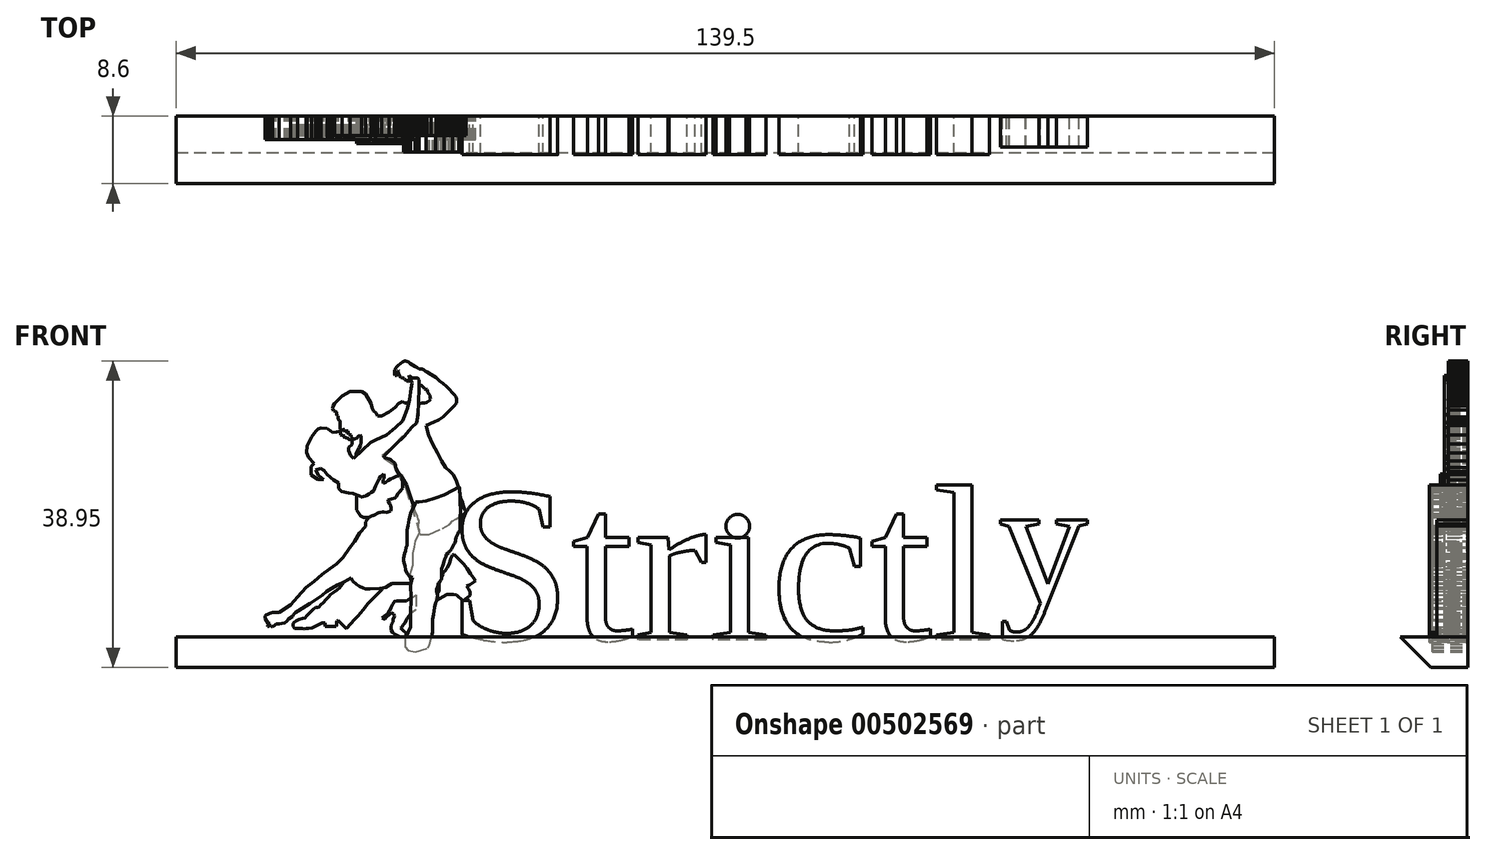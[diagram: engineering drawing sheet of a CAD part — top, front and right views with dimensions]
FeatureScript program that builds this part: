
annotation { "Feature Type Name" : "Feature", "Feature Type Description" : "" }
export const myFeature = defineFeature(function(context is Context, id is Id, definition is map)
    precondition{}
    {
        {
            var Q0;
            Q0=qCreatedBy(makeId("Front.planeOp"),FACE);
            var sketch = newSketch(context, id + "F0", { "sketchPlane" : qUnion([Q0])});
            skLineSegment(sketch, "E0", {"start": v(-53.06, 27.82) * mm, "end": v(-53.58, 27.08) * mm});
            skLineSegment(sketch, "E1", {"start": v(-53.58, 27.08) * mm, "end": v(-54.13, 25.96) * mm});
            skLineSegment(sketch, "E2", {"start": v(-54.13, 25.96) * mm, "end": v(-54.19, 25.15) * mm});
            skLineSegment(sketch, "E3", {"start": v(-54.19, 25.15) * mm, "end": v(-53.94, 24.5) * mm});
            skLineSegment(sketch, "E4", {"start": v(-53.94, 24.5) * mm, "end": v(-53.26, 23.7) * mm});
            skLineSegment(sketch, "E5", {"start": v(-53.26, 23.7) * mm, "end": v(-53.64, 23.37) * mm});
            skLineSegment(sketch, "E6", {"start": v(-53.64, 23.37) * mm, "end": v(-53.64, 22.67) * mm});
            skLineSegment(sketch, "E7", {"start": v(-53.64, 22.67) * mm, "end": v(-53.64, 22.27) * mm});
            skLineSegment(sketch, "E8", {"start": v(-53.64, 22.27) * mm, "end": v(-52.72, 21.68) * mm});
            skLineSegment(sketch, "E9", {"start": v(-52.72, 21.68) * mm, "end": v(-52.02, 21.68) * mm});
            skLineSegment(sketch, "E10", {"start": v(-52.02, 21.68) * mm, "end": v(-52.66, 22.2) * mm});
            skLineSegment(sketch, "E11", {"start": v(-52.66, 22.2) * mm, "end": v(-53.02, 22.89) * mm});
            skLineSegment(sketch, "E12", {"start": v(-53.02, 22.89) * mm, "end": v(-52.43, 23.06) * mm});
            skLineSegment(sketch, "E13", {"start": v(-52.43, 23.06) * mm, "end": v(-51.95, 22.82) * mm});
            skLineSegment(sketch, "E14", {"start": v(-51.95, 22.82) * mm, "end": v(-51.6, 22.35) * mm});
            skLineSegment(sketch, "E15", {"start": v(-51.6, 22.35) * mm, "end": v(-50.73, 21.64) * mm});
            skLineSegment(sketch, "E16", {"start": v(-50.73, 21.64) * mm, "end": v(-50.1, 21.27) * mm});
            skLineSegment(sketch, "E17", {"start": v(-50.1, 21.27) * mm, "end": v(-50.1, 20.97) * mm});
            skLineSegment(sketch, "E18", {"start": v(-50.1, 20.97) * mm, "end": v(-50.1, 20.53) * mm});
            skLineSegment(sketch, "E19", {"start": v(-50.1, 20.53) * mm, "end": v(-49.73, 20.2) * mm});
            skLineSegment(sketch, "E20", {"start": v(-49.73, 20.2) * mm, "end": v(-48.85, 20) * mm});
            skLineSegment(sketch, "E21", {"start": v(-48.85, 20) * mm, "end": v(-48.26, 19.9) * mm});
            skLineSegment(sketch, "E22", {"start": v(-48.26, 19.9) * mm, "end": v(-47.76, 19.67) * mm});
            skLineSegment(sketch, "E23", {"start": v(-47.76, 19.67) * mm, "end": v(-47.24, 19.46) * mm});
            skLineSegment(sketch, "E24", {"start": v(-47.24, 19.46) * mm, "end": v(-46.67, 19.58) * mm});
            skLineSegment(sketch, "E25", {"start": v(-46.67, 19.58) * mm, "end": v(-45.62, 20.23) * mm});
            skLineSegment(sketch, "E26", {"start": v(-45.62, 20.23) * mm, "end": v(-45.36, 20.9) * mm});
            skLineSegment(sketch, "E27", {"start": v(-45.36, 20.9) * mm, "end": v(-44.92, 21.82) * mm});
            skLineSegment(sketch, "E28", {"start": v(-44.92, 21.82) * mm, "end": v(-44.46, 22.36) * mm});
            skLineSegment(sketch, "E29", {"start": v(-44.46, 22.36) * mm, "end": v(-44.32, 22.24) * mm});
            skLineSegment(sketch, "E30", {"start": v(-44.32, 21.2) * mm, "end": v(-43.25, 21.86) * mm});
            skLineSegment(sketch, "E31", {"start": v(-43.25, 21.86) * mm, "end": v(-42.36, 22.24) * mm});
            skLineSegment(sketch, "E32", {"start": v(-42.36, 22.24) * mm, "end": v(-42.79, 23.01) * mm});
            skLineSegment(sketch, "E33", {"start": v(-42.79, 23.01) * mm, "end": v(-42.95, 23.7) * mm});
            skLineSegment(sketch, "E34", {"start": v(-42.95, 23.7) * mm, "end": v(-43.5, 24.23) * mm});
            skLineSegment(sketch, "E35", {"start": v(-43.5, 24.23) * mm, "end": v(-44.32, 24.46) * mm});
            skLineSegment(sketch, "E36", {"start": v(-44.32, 24.46) * mm, "end": v(-44.36, 24.68) * mm});
            skLineSegment(sketch, "E37", {"start": v(-44.36, 24.68) * mm, "end": v(-42.92, 26.08) * mm});
            skLineSegment(sketch, "E38", {"start": v(-42.92, 26.08) * mm, "end": v(-41.73, 27.23) * mm});
            skLineSegment(sketch, "E39", {"start": v(-41.73, 27.23) * mm, "end": v(-40.85, 28.27) * mm});
            skLineSegment(sketch, "E40", {"start": v(-40.85, 28.27) * mm, "end": v(-40.2, 28.88) * mm});
            skLineSegment(sketch, "E41", {"start": v(-40.2, 28.88) * mm, "end": v(-40.01, 29.93) * mm});
            skLineSegment(sketch, "E42", {"start": v(-40.01, 29.93) * mm, "end": v(-39.92, 33.22) * mm});
            skLineSegment(sketch, "E43", {"start": v(-39.92, 33.22) * mm, "end": v(-39.89, 34.32) * mm});
            skLineSegment(sketch, "E44", {"start": v(-39.89, 34.32) * mm, "end": v(-40.01, 34.54) * mm});
            skLineSegment(sketch, "E45", {"start": v(-40.01, 34.54) * mm, "end": v(-40.14, 34.59) * mm});
            skLineSegment(sketch, "E46", {"start": v(-40.14, 34.59) * mm, "end": v(-40.75, 34.61) * mm});
            skLineSegment(sketch, "E47", {"start": v(-40.75, 34.61) * mm, "end": v(-41.19, 34.9) * mm});
            skLineSegment(sketch, "E48", {"start": v(-41.19, 34.9) * mm, "end": v(-41.08, 34.46) * mm});
            skLineSegment(sketch, "E49", {"start": v(-41.08, 34.46) * mm, "end": v(-40.98, 34.36) * mm});
            skLineSegment(sketch, "E50", {"start": v(-40.98, 34.36) * mm, "end": v(-40.77, 33.93) * mm});
            skLineSegment(sketch, "E51", {"start": v(-40.77, 33.93) * mm, "end": v(-40.88, 33.22) * mm});
            skLineSegment(sketch, "E52", {"start": v(-40.88, 33.22) * mm, "end": v(-41.1, 31.86) * mm});
            skLineSegment(sketch, "E53", {"start": v(-41.1, 31.86) * mm, "end": v(-41.37, 30.75) * mm});
            skLineSegment(sketch, "E54", {"start": v(-41.37, 30.75) * mm, "end": v(-41.72, 29.75) * mm});
            skLineSegment(sketch, "E55", {"start": v(-41.72, 29.75) * mm, "end": v(-41.98, 29.15) * mm});
            skLineSegment(sketch, "E56", {"start": v(-41.98, 29.15) * mm, "end": v(-42.87, 28.32) * mm});
            skLineSegment(sketch, "E57", {"start": v(-42.87, 28.32) * mm, "end": v(-44.05, 27.37) * mm});
            skLineSegment(sketch, "E58", {"start": v(-44.05, 27.37) * mm, "end": v(-45.4, 26.73) * mm});
            skLineSegment(sketch, "E59", {"start": v(-45.4, 26.73) * mm, "end": v(-46.05, 26.38) * mm});
            skLineSegment(sketch, "E60", {"start": v(-46.05, 26.38) * mm, "end": v(-46.93, 25.56) * mm});
            skLineSegment(sketch, "E61", {"start": v(-46.93, 25.56) * mm, "end": v(-47.64, 24.9) * mm});
            skLineSegment(sketch, "E62", {"start": v(-47.64, 24.9) * mm, "end": v(-48.21, 24.35) * mm});
            skLineSegment(sketch, "E63", {"start": v(-48.21, 24.35) * mm, "end": v(-48.6, 24.76) * mm});
            skLineSegment(sketch, "E64", {"start": v(-48.6, 24.76) * mm, "end": v(-48.82, 25.34) * mm});
            skLineSegment(sketch, "E65", {"start": v(-48.82, 25.34) * mm, "end": v(-48.82, 25.78) * mm});
            skLineSegment(sketch, "E66", {"start": v(-48.82, 25.78) * mm, "end": v(-48.43, 26.16) * mm});
            skLineSegment(sketch, "E67", {"start": v(-48.43, 26.16) * mm, "end": v(-48.38, 26.51) * mm});
            skLineSegment(sketch, "E68", {"start": v(-48.38, 26.51) * mm, "end": v(-48.47, 26.69) * mm});
            skLineSegment(sketch, "E69", {"start": v(-48.47, 26.69) * mm, "end": v(-48.78, 26.74) * mm});
            skLineSegment(sketch, "E70", {"start": v(-48.78, 26.74) * mm, "end": v(-48.9, 26.87) * mm});
            skLineSegment(sketch, "E71", {"start": v(-48.9, 26.87) * mm, "end": v(-49.23, 27.04) * mm});
            skLineSegment(sketch, "E72", {"start": v(-49.23, 27.04) * mm, "end": v(-49.37, 26.9) * mm});
            skLineSegment(sketch, "E73", {"start": v(-49.37, 26.9) * mm, "end": v(-49.4, 27.21) * mm});
            skLineSegment(sketch, "E74", {"start": v(-49.4, 27.21) * mm, "end": v(-49.84, 27.32) * mm});
            skLineSegment(sketch, "E75", {"start": v(-49.84, 27.32) * mm, "end": v(-49.85, 27.76) * mm});
            skLineSegment(sketch, "E76", {"start": v(-49.85, 27.76) * mm, "end": v(-50.03, 27.79) * mm});
            skLineSegment(sketch, "E77", {"start": v(-50.4, 27.73) * mm, "end": v(-50.88, 27.63) * mm});
            skLineSegment(sketch, "E78", {"start": v(-50.88, 27.63) * mm, "end": v(-51.2, 27.89) * mm});
            skLineSegment(sketch, "E79", {"start": v(-51.2, 27.89) * mm, "end": v(-51.55, 28.14) * mm});
            skLineSegment(sketch, "E80", {"start": v(-51.55, 28.14) * mm, "end": v(-52.32, 28.23) * mm});
            skLineSegment(sketch, "E81", {"start": v(-52.32, 28.23) * mm, "end": v(-52.7, 28.13) * mm});
            skLineSegment(sketch, "E82", {"start": v(-52.7, 28.13) * mm, "end": v(-53.06, 27.82) * mm});
            skLineSegment(sketch, "E83", {"start": v(-50.03, 27.79) * mm, "end": v(-50.4, 27.73) * mm});
            skLineSegment(sketch, "E84", {"start": v(-44.32, 21.2) * mm, "end": v(-44.5, 21.2) * mm});
            skLineSegment(sketch, "E85", {"start": v(-44.5, 21.2) * mm, "end": v(-44.5, 21.47) * mm});
            skLineSegment(sketch, "E86", {"start": v(-44.5, 21.47) * mm, "end": v(-44.5, 21.6) * mm});
            skLineSegment(sketch, "E87", {"start": v(-44.5, 21.6) * mm, "end": v(-44.33, 21.82) * mm});
            skLineSegment(sketch, "E88", {"start": v(-44.33, 21.82) * mm, "end": v(-44.32, 22.24) * mm});
            skSolve(sketch);
        }
        {
            var Q0;
            Q0=makeQuery(id+"F0.imprint","IMPRINT",FACE,{"disambiguationData":[TD([[makeQuery(id+"F0.imprint","IMPRINT",EDGE,{"derivedFrom":sQuery(id+"F0.wireOp",EDGE,"E0")}),1.0]])]});
            extrude(context, id + "F1", {"entities" : qUnion([Q0]), "depth" : 3 * mm, "offsetDistance" : 25 * mm});
        }
        {
            var Q0;
            Q0=qCreatedBy(makeId("Front.planeOp"),FACE);
            var sketch = newSketch(context, id + "F2", { "sketchPlane" : qUnion([Q0])});
            skLineSegment(sketch, "E89", {"start": v(-46.21, 17.05) * mm, "end": v(-46.69, 16.29) * mm});
            skLineSegment(sketch, "E90", {"start": v(-46.69, 16.29) * mm, "end": v(-46.69, 15.72) * mm});
            skLineSegment(sketch, "E91", {"start": v(-46.69, 15.72) * mm, "end": v(-47.43, 14.93) * mm});
            skLineSegment(sketch, "E92", {"start": v(-47.43, 14.93) * mm, "end": v(-48.1, 13.82) * mm});
            skLineSegment(sketch, "E93", {"start": v(-48.1, 13.82) * mm, "end": v(-48.7, 12.97) * mm});
            skLineSegment(sketch, "E94", {"start": v(-48.7, 12.97) * mm, "end": v(-49.56, 11.77) * mm});
            skLineSegment(sketch, "E95", {"start": v(-49.56, 11.77) * mm, "end": v(-50.37, 10.98) * mm});
            skLineSegment(sketch, "E96", {"start": v(-50.37, 10.98) * mm, "end": v(-51.28, 10.32) * mm});
            skLineSegment(sketch, "E97", {"start": v(-51.28, 10.32) * mm, "end": v(-52.23, 9.62) * mm});
            skLineSegment(sketch, "E98", {"start": v(-52.23, 9.62) * mm, "end": v(-53.24, 8.75) * mm});
            skLineSegment(sketch, "E99", {"start": v(-53.24, 8.75) * mm, "end": v(-54.28, 7.99) * mm});
            skLineSegment(sketch, "E100", {"start": v(-54.28, 7.99) * mm, "end": v(-55.36, 6.8) * mm});
            skLineSegment(sketch, "E101", {"start": v(-55.36, 6.8) * mm, "end": v(-56.24, 5.77) * mm});
            skLineSegment(sketch, "E102", {"start": v(-56.24, 5.77) * mm, "end": v(-57.11, 5.18) * mm});
            skLineSegment(sketch, "E103", {"start": v(-57.11, 5.18) * mm, "end": v(-57.7, 4.79) * mm});
            skLineSegment(sketch, "E104", {"start": v(-57.7, 4.79) * mm, "end": v(-57.98, 4.79) * mm});
            skLineSegment(sketch, "E105", {"start": v(-57.98, 4.79) * mm, "end": v(-58.5, 4.79) * mm});
            skLineSegment(sketch, "E106", {"start": v(-58.5, 4.79) * mm, "end": v(-58.9, 4.7) * mm});
            skLineSegment(sketch, "E107", {"start": v(-58.9, 4.7) * mm, "end": v(-59.11, 4.56) * mm});
            skLineSegment(sketch, "E108", {"start": v(-59.11, 4.56) * mm, "end": v(-59.33, 4.5) * mm});
            skLineSegment(sketch, "E109", {"start": v(-59.33, 4.5) * mm, "end": v(-59.48, 4.39) * mm});
            skLineSegment(sketch, "E110", {"start": v(-59.48, 4.39) * mm, "end": v(-59.48, 4.02) * mm});
            skLineSegment(sketch, "E111", {"start": v(-59.48, 4.02) * mm, "end": v(-59.16, 3.54) * mm});
            skLineSegment(sketch, "E112", {"start": v(-59.16, 3.54) * mm, "end": v(-59.05, 3.38) * mm});
            skLineSegment(sketch, "E113", {"start": v(-59.05, 3.38) * mm, "end": v(-58.83, 3.38) * mm});
            skLineSegment(sketch, "E114", {"start": v(-58.83, 3.38) * mm, "end": v(-59.17, 3.16) * mm});
            skLineSegment(sketch, "E115", {"start": v(-59.17, 3.16) * mm, "end": v(-59.12, 3.01) * mm});
            skLineSegment(sketch, "E116", {"start": v(-59.12, 3.01) * mm, "end": v(-58.95, 3.01) * mm});
            skLineSegment(sketch, "E117", {"start": v(-58.95, 3.01) * mm, "end": v(-58.8, 3.12) * mm});
            skLineSegment(sketch, "E118", {"start": v(-58.8, 3.12) * mm, "end": v(-58.72, 3.16) * mm});
            skLineSegment(sketch, "E119", {"start": v(-58.72, 3.16) * mm, "end": v(-58.65, 3.01) * mm});
            skLineSegment(sketch, "E120", {"start": v(-58.65, 3.01) * mm, "end": v(-58.5, 2.97) * mm});
            skLineSegment(sketch, "E121", {"start": v(-58.5, 2.97) * mm, "end": v(-58.33, 3.07) * mm});
            skLineSegment(sketch, "E122", {"start": v(-58.33, 3.07) * mm, "end": v(-58.04, 3.32) * mm});
            skLineSegment(sketch, "E123", {"start": v(-58.04, 3.32) * mm, "end": v(-57.65, 3.37) * mm});
            skLineSegment(sketch, "E124", {"start": v(-57.65, 3.37) * mm, "end": v(-56.98, 3.5) * mm});
            skLineSegment(sketch, "E125", {"start": v(-56.98, 3.5) * mm, "end": v(-56.7, 3.64) * mm});
            skLineSegment(sketch, "E126", {"start": v(-56.7, 3.64) * mm, "end": v(-56.45, 3.99) * mm});
            skLineSegment(sketch, "E127", {"start": v(-56.45, 3.99) * mm, "end": v(-55.97, 4.3) * mm});
            skLineSegment(sketch, "E128", {"start": v(-55.97, 4.3) * mm, "end": v(-55.86, 4.56) * mm});
            skLineSegment(sketch, "E129", {"start": v(-55.86, 4.56) * mm, "end": v(-55.57, 4.82) * mm});
            skLineSegment(sketch, "E130", {"start": v(-55.57, 4.82) * mm, "end": v(-55.27, 5) * mm});
            skLineSegment(sketch, "E131", {"start": v(-55.27, 5) * mm, "end": v(-53.75, 5.93) * mm});
            skLineSegment(sketch, "E132", {"start": v(-53.75, 5.93) * mm, "end": v(-53.02, 6.42) * mm});
            skLineSegment(sketch, "E133", {"start": v(-53.02, 6.42) * mm, "end": v(-52.24, 6.94) * mm});
            skLineSegment(sketch, "E134", {"start": v(-52.24, 6.94) * mm, "end": v(-51.63, 7.46) * mm});
            skLineSegment(sketch, "E135", {"start": v(-51.63, 7.46) * mm, "end": v(-51, 7.88) * mm});
            skLineSegment(sketch, "E136", {"start": v(-51, 7.88) * mm, "end": v(-50.27, 8.3) * mm});
            skLineSegment(sketch, "E137", {"start": v(-50.27, 8.3) * mm, "end": v(-49.73, 8.54) * mm});
            skLineSegment(sketch, "E138", {"start": v(-49.73, 8.54) * mm, "end": v(-49.4, 8.68) * mm});
            skLineSegment(sketch, "E139", {"start": v(-49.4, 8.68) * mm, "end": v(-48.51, 9.16) * mm});
            skLineSegment(sketch, "E140", {"start": v(-48.51, 9.16) * mm, "end": v(-48.3, 8.78) * mm});
            skLineSegment(sketch, "E141", {"start": v(-48.3, 8.78) * mm, "end": v(-47.85, 8.37) * mm});
            skLineSegment(sketch, "E142", {"start": v(-47.85, 8.37) * mm, "end": v(-47.48, 8.12) * mm});
            skLineSegment(sketch, "E143", {"start": v(-47.48, 8.12) * mm, "end": v(-47.03, 7.94) * mm});
            skLineSegment(sketch, "E144", {"start": v(-47.03, 7.94) * mm, "end": v(-46.67, 7.81) * mm});
            skLineSegment(sketch, "E145", {"start": v(-46.67, 7.81) * mm, "end": v(-46.1, 7.81) * mm});
            skLineSegment(sketch, "E146", {"start": v(-46.1, 7.81) * mm, "end": v(-44.84, 7.86) * mm});
            skLineSegment(sketch, "E147", {"start": v(-44.84, 7.86) * mm, "end": v(-44.17, 8) * mm});
            skLineSegment(sketch, "E148", {"start": v(-44.17, 8) * mm, "end": v(-43.66, 8.27) * mm});
            skLineSegment(sketch, "E149", {"start": v(-43.66, 8.27) * mm, "end": v(-43.35, 8.48) * mm});
            skLineSegment(sketch, "E150", {"start": v(-43.35, 8.48) * mm, "end": v(-42.47, 8.48) * mm});
            skLineSegment(sketch, "E151", {"start": v(-42.47, 8.48) * mm, "end": v(-41.17, 8.48) * mm});
            skLineSegment(sketch, "E152", {"start": v(-41.17, 8.48) * mm, "end": v(-40.8, 8.38) * mm});
            skLineSegment(sketch, "E153", {"start": v(-40.8, 8.38) * mm, "end": v(-40.89, 8.88) * mm});
            skLineSegment(sketch, "E154", {"start": v(-40.89, 8.88) * mm, "end": v(-41.02, 9.33) * mm});
            skLineSegment(sketch, "E155", {"start": v(-41.02, 9.33) * mm, "end": v(-40.9, 10) * mm});
            skLineSegment(sketch, "E156", {"start": v(-40.9, 10) * mm, "end": v(-40.67, 10.82) * mm});
            skLineSegment(sketch, "E157", {"start": v(-40.67, 10.82) * mm, "end": v(-40.67, 11.56) * mm});
            skLineSegment(sketch, "E158", {"start": v(-40.67, 11.56) * mm, "end": v(-40.67, 12.27) * mm});
            skLineSegment(sketch, "E159", {"start": v(-40.67, 12.27) * mm, "end": v(-40.5, 13.12) * mm});
            skLineSegment(sketch, "E160", {"start": v(-40.5, 13.12) * mm, "end": v(-40.33, 13.9) * mm});
            skLineSegment(sketch, "E161", {"start": v(-40.33, 13.9) * mm, "end": v(-39.8, 15) * mm});
            skLineSegment(sketch, "E162", {"start": v(-39.8, 15) * mm, "end": v(-39.8, 15.3) * mm});
            skLineSegment(sketch, "E163", {"start": v(-39.8, 15.3) * mm, "end": v(-39.98, 15.54) * mm});
            skLineSegment(sketch, "E164", {"start": v(-39.98, 15.54) * mm, "end": v(-39.98, 15.89) * mm});
            skLineSegment(sketch, "E165", {"start": v(-39.98, 15.89) * mm, "end": v(-39.89, 16.17) * mm});
            skLineSegment(sketch, "E166", {"start": v(-39.89, 16.17) * mm, "end": v(-39.89, 16.5) * mm});
            skLineSegment(sketch, "E167", {"start": v(-39.89, 16.5) * mm, "end": v(-40.02, 16.7) * mm});
            skLineSegment(sketch, "E168", {"start": v(-40.02, 16.7) * mm, "end": v(-40.11, 17.01) * mm});
            skLineSegment(sketch, "E169", {"start": v(-40.11, 17.01) * mm, "end": v(-40.4, 17.72) * mm});
            skLineSegment(sketch, "E170", {"start": v(-40.4, 17.72) * mm, "end": v(-40.69, 18.51) * mm});
            skLineSegment(sketch, "E171", {"start": v(-40.69, 18.51) * mm, "end": v(-40.88, 19.14) * mm});
            skLineSegment(sketch, "E172", {"start": v(-40.88, 19.14) * mm, "end": v(-41.11, 19.88) * mm});
            skLineSegment(sketch, "E173", {"start": v(-41.11, 19.88) * mm, "end": v(-41.33, 20.55) * mm});
            skLineSegment(sketch, "E174", {"start": v(-41.33, 20.55) * mm, "end": v(-41.47, 21.02) * mm});
            skLineSegment(sketch, "E175", {"start": v(-41.47, 21.02) * mm, "end": v(-41.8, 21.5) * mm});
            skLineSegment(sketch, "E176", {"start": v(-41.8, 21.5) * mm, "end": v(-42.09, 21.93) * mm});
            skLineSegment(sketch, "E177", {"start": v(-42.09, 21.93) * mm, "end": v(-41.98, 20.95) * mm});
            skLineSegment(sketch, "E178", {"start": v(-41.98, 20.95) * mm, "end": v(-41.98, 20.52) * mm});
            skLineSegment(sketch, "E179", {"start": v(-41.98, 20.52) * mm, "end": v(-42.34, 20.27) * mm});
            skLineSegment(sketch, "E180", {"start": v(-42.34, 20.27) * mm, "end": v(-42.73, 19.69) * mm});
            skLineSegment(sketch, "E181", {"start": v(-42.73, 19.69) * mm, "end": v(-42.97, 19.36) * mm});
            skLineSegment(sketch, "E182", {"start": v(-42.97, 19.36) * mm, "end": v(-43.46, 19.2) * mm});
            skLineSegment(sketch, "E183", {"start": v(-43.46, 19.2) * mm, "end": v(-43.9, 19.07) * mm});
            skLineSegment(sketch, "E184", {"start": v(-43.9, 19.07) * mm, "end": v(-43.61, 18.63) * mm});
            skLineSegment(sketch, "E185", {"start": v(-43.61, 18.63) * mm, "end": v(-43.48, 18.22) * mm});
            skLineSegment(sketch, "E186", {"start": v(-43.48, 18.22) * mm, "end": v(-43.48, 17.8) * mm});
            skLineSegment(sketch, "E187", {"start": v(-43.48, 17.8) * mm, "end": v(-43.67, 17.68) * mm});
            skLineSegment(sketch, "E188", {"start": v(-43.67, 17.68) * mm, "end": v(-43.96, 17.56) * mm});
            skLineSegment(sketch, "E189", {"start": v(-43.96, 17.56) * mm, "end": v(-44.45, 17.56) * mm});
            skLineSegment(sketch, "E190", {"start": v(-44.45, 17.56) * mm, "end": v(-44.95, 17.57) * mm});
            skLineSegment(sketch, "E191", {"start": v(-44.95, 17.57) * mm, "end": v(-45.2, 17.4) * mm});
            skLineSegment(sketch, "E192", {"start": v(-45.2, 17.4) * mm, "end": v(-45.6, 17.13) * mm});
            skLineSegment(sketch, "E193", {"start": v(-45.6, 17.13) * mm, "end": v(-46.21, 17.05) * mm});
            skSolve(sketch);
        }
        {
            var Q0;
            Q0=makeQuery(id+"F2.imprint","IMPRINT",FACE,{"disambiguationData":[TD([[makeQuery(id+"F2.imprint","IMPRINT",EDGE,{"derivedFrom":sQuery(id+"F2.wireOp",EDGE,"E89")}),1.0]])]});
            extrude(context, id + "F3", {"entities" : qUnion([Q0]), "depth" : 3 * mm, "offsetDistance" : 25 * mm});
        }
        {
            var Q0;
            Q0=qCreatedBy(makeId("Front.planeOp"),FACE);
            var sketch = newSketch(context, id + "F4", { "sketchPlane" : qUnion([Q0])});
            skLineSegment(sketch, "E194", {"start": v(-40.43, 5.05) * mm, "end": v(-40.9, 4.7) * mm});
            skLineSegment(sketch, "E195", {"start": v(-40.9, 4.7) * mm, "end": v(-41.22, 4.32) * mm});
            skLineSegment(sketch, "E196", {"start": v(-41.22, 4.32) * mm, "end": v(-41.42, 4.06) * mm});
            skLineSegment(sketch, "E197", {"start": v(-41.42, 4.06) * mm, "end": v(-41.55, 3.76) * mm});
            skLineSegment(sketch, "E198", {"start": v(-41.55, 3.76) * mm, "end": v(-41.7, 3.45) * mm});
            skLineSegment(sketch, "E199", {"start": v(-41.7, 3.45) * mm, "end": v(-41.92, 3.2) * mm});
            skLineSegment(sketch, "E200", {"start": v(-41.92, 3.2) * mm, "end": v(-42.08, 2.97) * mm});
            skLineSegment(sketch, "E201", {"start": v(-42.08, 2.97) * mm, "end": v(-42.22, 2.83) * mm});
            skLineSegment(sketch, "E202", {"start": v(-42.22, 2.83) * mm, "end": v(-42.16, 2.76) * mm});
            skLineSegment(sketch, "E203", {"start": v(-42.16, 2.76) * mm, "end": v(-41.83, 2.46) * mm});
            skLineSegment(sketch, "E204", {"start": v(-41.83, 2.46) * mm, "end": v(-41.58, 2.2) * mm});
            skLineSegment(sketch, "E205", {"start": v(-41.58, 2.2) * mm, "end": v(-41.58, 1.8) * mm});
            skLineSegment(sketch, "E206", {"start": v(-41.58, 1.8) * mm, "end": v(-41.87, 1.7) * mm});
            skLineSegment(sketch, "E207", {"start": v(-41.87, 1.7) * mm, "end": v(-42.23, 1.7) * mm});
            skLineSegment(sketch, "E208", {"start": v(-42.23, 1.7) * mm, "end": v(-42.55, 1.8) * mm});
            skLineSegment(sketch, "E209", {"start": v(-42.55, 1.8) * mm, "end": v(-42.94, 2.02) * mm});
            skLineSegment(sketch, "E210", {"start": v(-42.94, 2.02) * mm, "end": v(-43.24, 2.27) * mm});
            skLineSegment(sketch, "E211", {"start": v(-43.24, 2.27) * mm, "end": v(-43.46, 2.6) * mm});
            skLineSegment(sketch, "E212", {"start": v(-43.46, 2.6) * mm, "end": v(-43.46, 2.94) * mm});
            skLineSegment(sketch, "E213", {"start": v(-43.46, 2.94) * mm, "end": v(-43.38, 3.32) * mm});
            skLineSegment(sketch, "E214", {"start": v(-43.38, 3.32) * mm, "end": v(-43.21, 3.62) * mm});
            skLineSegment(sketch, "E215", {"start": v(-43.21, 3.62) * mm, "end": v(-43.21, 3.92) * mm});
            skLineSegment(sketch, "E216", {"start": v(-43.21, 3.92) * mm, "end": v(-43, 4.36) * mm});
            skLineSegment(sketch, "E217", {"start": v(-43, 4.36) * mm, "end": v(-43.13, 4.63) * mm});
            skLineSegment(sketch, "E218", {"start": v(-43.13, 4.63) * mm, "end": v(-43.36, 4.75) * mm});
            skLineSegment(sketch, "E219", {"start": v(-43.36, 4.75) * mm, "end": v(-43.67, 4.54) * mm});
            skLineSegment(sketch, "E220", {"start": v(-43.67, 4.54) * mm, "end": v(-44, 4.26) * mm});
            skLineSegment(sketch, "E221", {"start": v(-44, 4.26) * mm, "end": v(-44.24, 3.97) * mm});
            skLineSegment(sketch, "E222", {"start": v(-44.24, 3.97) * mm, "end": v(-44.37, 3.97) * mm});
            skLineSegment(sketch, "E223", {"start": v(-44.37, 3.97) * mm, "end": v(-44.6, 4.09) * mm});
            skLineSegment(sketch, "E224", {"start": v(-44.6, 4.09) * mm, "end": v(-44.21, 4.45) * mm});
            skLineSegment(sketch, "E225", {"start": v(-44.21, 4.45) * mm, "end": v(-43.82, 4.68) * mm});
            skLineSegment(sketch, "E226", {"start": v(-43.82, 4.68) * mm, "end": v(-43.64, 5) * mm});
            skLineSegment(sketch, "E227", {"start": v(-43.64, 5) * mm, "end": v(-43.45, 5.44) * mm});
            skLineSegment(sketch, "E228", {"start": v(-43.45, 5.44) * mm, "end": v(-43.26, 5.85) * mm});
            skLineSegment(sketch, "E229", {"start": v(-43.26, 5.85) * mm, "end": v(-43.02, 6.17) * mm});
            skLineSegment(sketch, "E230", {"start": v(-43.02, 6.17) * mm, "end": v(-42.66, 6.26) * mm});
            skLineSegment(sketch, "E231", {"start": v(-42.66, 6.26) * mm, "end": v(-42.2, 6.26) * mm});
            skLineSegment(sketch, "E232", {"start": v(-42.2, 6.26) * mm, "end": v(-41.48, 6.26) * mm});
            skLineSegment(sketch, "E233", {"start": v(-41.48, 6.26) * mm, "end": v(-41.06, 6.56) * mm});
            skLineSegment(sketch, "E234", {"start": v(-41.06, 6.56) * mm, "end": v(-40.66, 6.8) * mm});
            skLineSegment(sketch, "E235", {"start": v(-40.66, 6.8) * mm, "end": v(-40.3, 7.04) * mm});
            skLineSegment(sketch, "E236", {"start": v(-40.3, 7.04) * mm, "end": v(-40.3, 6.42) * mm});
            skLineSegment(sketch, "E237", {"start": v(-40.3, 6.42) * mm, "end": v(-40.3, 5.92) * mm});
            skLineSegment(sketch, "E238", {"start": v(-40.3, 5.92) * mm, "end": v(-40.3, 5.48) * mm});
            skLineSegment(sketch, "E239", {"start": v(-40.3, 5.48) * mm, "end": v(-40.3, 5.15) * mm});
            skLineSegment(sketch, "E240", {"start": v(-40.3, 5.15) * mm, "end": v(-40.43, 5.05) * mm});
            skSolve(sketch);
        }
        {
            var Q0;
            Q0=makeQuery(id+"F4.imprint","IMPRINT",FACE,{"disambiguationData":[TD([[makeQuery(id+"F4.imprint","IMPRINT",EDGE,{"derivedFrom":sQuery(id+"F4.wireOp",EDGE,"E194")}),-1.0]])]});
            extrude(context, id + "F5", {"entities" : qUnion([Q0]), "depth" : 3 * mm, "offsetDistance" : 25 * mm});
        }
        {
            var Q0;
            Q0=qCreatedBy(makeId("Front.planeOp"),FACE);
            var sketch = newSketch(context, id + "F6", { "sketchPlane" : qUnion([Q0])});
            skLineSegment(sketch, "E241", {"start": v(-35.64, 12.13) * mm, "end": v(-35.88, 11.56) * mm});
            skLineSegment(sketch, "E242", {"start": v(-35.88, 11.56) * mm, "end": v(-36.04, 11) * mm});
            skLineSegment(sketch, "E243", {"start": v(-36.04, 11) * mm, "end": v(-36.34, 10.44) * mm});
            skLineSegment(sketch, "E244", {"start": v(-36.34, 10.44) * mm, "end": v(-36.6, 10.1) * mm});
            skLineSegment(sketch, "E245", {"start": v(-36.6, 10.1) * mm, "end": v(-36.87, 9.91) * mm});
            skLineSegment(sketch, "E246", {"start": v(-36.87, 9.66) * mm, "end": v(-37, 9.38) * mm});
            skLineSegment(sketch, "E247", {"start": v(-37, 9.38) * mm, "end": v(-37.15, 8.86) * mm});
            skLineSegment(sketch, "E248", {"start": v(-37.15, 8.86) * mm, "end": v(-37.33, 8.48) * mm});
            skLineSegment(sketch, "E249", {"start": v(-37.33, 8.48) * mm, "end": v(-37.33, 7.98) * mm});
            skLineSegment(sketch, "E250", {"start": v(-37.33, 7.98) * mm, "end": v(-37.33, 7.48) * mm});
            skLineSegment(sketch, "E251", {"start": v(-37.33, 7.48) * mm, "end": v(-37.6, 7.1) * mm});
            skLineSegment(sketch, "E252", {"start": v(-37.6, 7.1) * mm, "end": v(-37.79, 6.52) * mm});
            skLineSegment(sketch, "E253", {"start": v(-37.79, 6.52) * mm, "end": v(-37.79, 6.18) * mm});
            skLineSegment(sketch, "E254", {"start": v(-37.79, 6.18) * mm, "end": v(-37.33, 6.54) * mm});
            skLineSegment(sketch, "E255", {"start": v(-37.33, 6.54) * mm, "end": v(-36.35, 7.11) * mm});
            skLineSegment(sketch, "E256", {"start": v(-36.35, 7.11) * mm, "end": v(-35.98, 7.11) * mm});
            skLineSegment(sketch, "E257", {"start": v(-35.98, 7.11) * mm, "end": v(-35.52, 7.11) * mm});
            skLineSegment(sketch, "E258", {"start": v(-35.52, 7.11) * mm, "end": v(-35.12, 7) * mm});
            skLineSegment(sketch, "E259", {"start": v(-35.12, 7) * mm, "end": v(-34.86, 6.77) * mm});
            skLineSegment(sketch, "E260", {"start": v(-34.86, 6.77) * mm, "end": v(-34.56, 6.52) * mm});
            skLineSegment(sketch, "E261", {"start": v(-34.56, 6.52) * mm, "end": v(-34.3, 6.24) * mm});
            skLineSegment(sketch, "E262", {"start": v(-34.3, 6.24) * mm, "end": v(-34, 6.5) * mm});
            skLineSegment(sketch, "E263", {"start": v(-34, 6.5) * mm, "end": v(-33.73, 6.7) * mm});
            skLineSegment(sketch, "E264", {"start": v(-33.73, 6.7) * mm, "end": v(-33.44, 7) * mm});
            skLineSegment(sketch, "E265", {"start": v(-33.44, 7) * mm, "end": v(-33.44, 7.42) * mm});
            skLineSegment(sketch, "E266", {"start": v(-33.44, 7.42) * mm, "end": v(-33.6, 7.82) * mm});
            skLineSegment(sketch, "E267", {"start": v(-33.6, 7.82) * mm, "end": v(-33.86, 8.15) * mm});
            skLineSegment(sketch, "E268", {"start": v(-33.86, 8.15) * mm, "end": v(-33.46, 8.3) * mm});
            skLineSegment(sketch, "E269", {"start": v(-33.46, 8.3) * mm, "end": v(-33.12, 8.54) * mm});
            skLineSegment(sketch, "E270", {"start": v(-33.12, 8.54) * mm, "end": v(-32.73, 8.78) * mm});
            skLineSegment(sketch, "E271", {"start": v(-32.73, 8.78) * mm, "end": v(-32.98, 9.21) * mm});
            skLineSegment(sketch, "E272", {"start": v(-32.98, 9.21) * mm, "end": v(-33.37, 9.72) * mm});
            skLineSegment(sketch, "E273", {"start": v(-33.37, 9.72) * mm, "end": v(-33.83, 10.4) * mm});
            skLineSegment(sketch, "E274", {"start": v(-33.83, 10.4) * mm, "end": v(-34.25, 10.94) * mm});
            skLineSegment(sketch, "E275", {"start": v(-34.25, 10.94) * mm, "end": v(-34.8, 11.53) * mm});
            skLineSegment(sketch, "E276", {"start": v(-34.8, 11.53) * mm, "end": v(-35.13, 11.87) * mm});
            skLineSegment(sketch, "E277", {"start": v(-35.13, 11.87) * mm, "end": v(-35.47, 12.15) * mm});
            skLineSegment(sketch, "E278", {"start": v(-35.47, 12.15) * mm, "end": v(-35.64, 12.13) * mm});
            skLineSegment(sketch, "E279", {"start": v(-36.87, 9.91) * mm, "end": v(-36.87, 9.66) * mm});
            skSolve(sketch);
        }
        {
            var Q0;
            Q0=makeQuery(id+"F6.imprint","IMPRINT",FACE,{"disambiguationData":[TD([[makeQuery(id+"F6.imprint","IMPRINT",EDGE,{"derivedFrom":sQuery(id+"F6.wireOp",EDGE,"E241")}),1.0]])]});
            extrude(context, id + "F7", {"entities" : qUnion([Q0]), "depth" : 3 * mm, "offsetDistance" : 25 * mm});
        }
        {
            var Q0;
            Q0=qCreatedBy(makeId("Front.planeOp"),FACE);
            var sketch = newSketch(context, id + "F8", { "sketchPlane" : qUnion([Q0])});
            skLineSegment(sketch, "E280", {"start": v(-47.86, 19.72) * mm, "end": v(-47.86, 19.29) * mm});
            skLineSegment(sketch, "E281", {"start": v(-47.86, 19.29) * mm, "end": v(-47.86, 18.79) * mm});
            skLineSegment(sketch, "E282", {"start": v(-47.86, 18.79) * mm, "end": v(-47.86, 18.3) * mm});
            skLineSegment(sketch, "E283", {"start": v(-47.86, 18.3) * mm, "end": v(-47.86, 17.82) * mm});
            skLineSegment(sketch, "E284", {"start": v(-47.86, 17.82) * mm, "end": v(-47.58, 17.45) * mm});
            skLineSegment(sketch, "E285", {"start": v(-47.58, 17.45) * mm, "end": v(-47.35, 17.04) * mm});
            skLineSegment(sketch, "E286", {"start": v(-47.35, 17.04) * mm, "end": v(-46.94, 16.84) * mm});
            skLineSegment(sketch, "E287", {"start": v(-46.94, 16.84) * mm, "end": v(-46.51, 16.84) * mm});
            skLineSegment(sketch, "E288", {"start": v(-46.51, 16.84) * mm, "end": v(-46.17, 16.84) * mm});
            skLineSegment(sketch, "E289", {"start": v(-46.17, 16.84) * mm, "end": v(-45.95, 17.06) * mm});
            skLineSegment(sketch, "E290", {"start": v(-45.95, 17.06) * mm, "end": v(-45.53, 17.18) * mm});
            skLineSegment(sketch, "E291", {"start": v(-45.53, 17.18) * mm, "end": v(-45.08, 17.45) * mm});
            skLineSegment(sketch, "E292", {"start": v(-45.08, 17.45) * mm, "end": v(-44.56, 17.58) * mm});
            skLineSegment(sketch, "E293", {"start": v(-44.56, 17.58) * mm, "end": v(-44.04, 17.53) * mm});
            skLineSegment(sketch, "E294", {"start": v(-44.04, 17.53) * mm, "end": v(-43.67, 17.64) * mm});
            skLineSegment(sketch, "E295", {"start": v(-43.67, 17.64) * mm, "end": v(-43.53, 17.72) * mm});
            skLineSegment(sketch, "E296", {"start": v(-43.53, 17.72) * mm, "end": v(-43.44, 17.84) * mm});
            skLineSegment(sketch, "E297", {"start": v(-43.44, 17.84) * mm, "end": v(-43.44, 18.1) * mm});
            skLineSegment(sketch, "E298", {"start": v(-43.44, 18.1) * mm, "end": v(-43.5, 18.38) * mm});
            skLineSegment(sketch, "E299", {"start": v(-43.5, 18.38) * mm, "end": v(-43.61, 18.67) * mm});
            skLineSegment(sketch, "E300", {"start": v(-43.61, 18.67) * mm, "end": v(-43.83, 19) * mm});
            skLineSegment(sketch, "E301", {"start": v(-43.83, 19) * mm, "end": v(-43.83, 19.08) * mm});
            skLineSegment(sketch, "E302", {"start": v(-43.83, 19.08) * mm, "end": v(-42.95, 19.33) * mm});
            skLineSegment(sketch, "E303", {"start": v(-42.95, 19.33) * mm, "end": v(-42.8, 19.47) * mm});
            skLineSegment(sketch, "E304", {"start": v(-42.8, 19.47) * mm, "end": v(-42.57, 19.88) * mm});
            skLineSegment(sketch, "E305", {"start": v(-42.57, 19.88) * mm, "end": v(-42.25, 20.26) * mm});
            skLineSegment(sketch, "E306", {"start": v(-42.25, 20.26) * mm, "end": v(-41.96, 20.6) * mm});
            skLineSegment(sketch, "E307", {"start": v(-41.96, 20.6) * mm, "end": v(-41.96, 20.83) * mm});
            skLineSegment(sketch, "E308", {"start": v(-41.96, 20.83) * mm, "end": v(-41.96, 21.3) * mm});
            skLineSegment(sketch, "E309", {"start": v(-41.96, 21.3) * mm, "end": v(-42.03, 21.7) * mm});
            skLineSegment(sketch, "E310", {"start": v(-42.03, 21.7) * mm, "end": v(-42.09, 21.97) * mm});
            skLineSegment(sketch, "E311", {"start": v(-42.09, 21.97) * mm, "end": v(-42.15, 22.2) * mm});
            skLineSegment(sketch, "E312", {"start": v(-42.15, 22.2) * mm, "end": v(-42.32, 22.32) * mm});
            skLineSegment(sketch, "E313", {"start": v(-42.32, 22.32) * mm, "end": v(-42.5, 22.22) * mm});
            skLineSegment(sketch, "E314", {"start": v(-42.5, 22.22) * mm, "end": v(-42.95, 22.04) * mm});
            skLineSegment(sketch, "E315", {"start": v(-42.95, 22.04) * mm, "end": v(-43.2, 21.9) * mm});
            skLineSegment(sketch, "E316", {"start": v(-43.2, 21.9) * mm, "end": v(-43.5, 21.75) * mm});
            skLineSegment(sketch, "E317", {"start": v(-43.5, 21.75) * mm, "end": v(-43.82, 21.55) * mm});
            skLineSegment(sketch, "E318", {"start": v(-43.82, 21.55) * mm, "end": v(-44.13, 21.33) * mm});
            skLineSegment(sketch, "E319", {"start": v(-44.13, 21.33) * mm, "end": v(-44.32, 21.23) * mm});
            skLineSegment(sketch, "E320", {"start": v(-44.32, 21.23) * mm, "end": v(-44.43, 21.23) * mm});
            skLineSegment(sketch, "E321", {"start": v(-44.43, 21.23) * mm, "end": v(-44.49, 21.44) * mm});
            skLineSegment(sketch, "E322", {"start": v(-44.49, 21.44) * mm, "end": v(-44.49, 21.61) * mm});
            skLineSegment(sketch, "E323", {"start": v(-44.49, 21.61) * mm, "end": v(-44.32, 21.84) * mm});
            skLineSegment(sketch, "E324", {"start": v(-44.32, 21.84) * mm, "end": v(-44.32, 22.28) * mm});
            skLineSegment(sketch, "E325", {"start": v(-44.32, 22.28) * mm, "end": v(-44.43, 22.4) * mm});
            skLineSegment(sketch, "E326", {"start": v(-44.43, 22.4) * mm, "end": v(-44.5, 22.33) * mm});
            skLineSegment(sketch, "E327", {"start": v(-44.5, 22.33) * mm, "end": v(-44.79, 22.05) * mm});
            skLineSegment(sketch, "E328", {"start": v(-44.79, 22.05) * mm, "end": v(-44.98, 21.78) * mm});
            skLineSegment(sketch, "E329", {"start": v(-44.98, 21.78) * mm, "end": v(-45.16, 21.38) * mm});
            skLineSegment(sketch, "E330", {"start": v(-45.16, 21.38) * mm, "end": v(-45.4, 20.9) * mm});
            skLineSegment(sketch, "E331", {"start": v(-45.4, 20.9) * mm, "end": v(-45.54, 20.53) * mm});
            skLineSegment(sketch, "E332", {"start": v(-45.54, 20.53) * mm, "end": v(-45.64, 20.25) * mm});
            skLineSegment(sketch, "E333", {"start": v(-45.64, 20.25) * mm, "end": v(-45.96, 20.04) * mm});
            skLineSegment(sketch, "E334", {"start": v(-45.96, 20.04) * mm, "end": v(-46.26, 19.84) * mm});
            skLineSegment(sketch, "E335", {"start": v(-46.26, 19.84) * mm, "end": v(-46.56, 19.66) * mm});
            skLineSegment(sketch, "E336", {"start": v(-46.56, 19.66) * mm, "end": v(-46.7, 19.58) * mm});
            skLineSegment(sketch, "E337", {"start": v(-46.7, 19.58) * mm, "end": v(-46.92, 19.55) * mm});
            skLineSegment(sketch, "E338", {"start": v(-46.92, 19.55) * mm, "end": v(-47.17, 19.49) * mm});
            skLineSegment(sketch, "E339", {"start": v(-47.17, 19.49) * mm, "end": v(-47.24, 19.47) * mm});
            skLineSegment(sketch, "E340", {"start": v(-47.24, 19.47) * mm, "end": v(-47.29, 19.49) * mm});
            skLineSegment(sketch, "E341", {"start": v(-47.29, 19.49) * mm, "end": v(-47.47, 19.58) * mm});
            skLineSegment(sketch, "E342", {"start": v(-47.47, 19.58) * mm, "end": v(-47.63, 19.64) * mm});
            skLineSegment(sketch, "E343", {"start": v(-47.63, 19.64) * mm, "end": v(-47.72, 19.68) * mm});
            skLineSegment(sketch, "E344", {"start": v(-47.72, 19.68) * mm, "end": v(-47.8, 19.7) * mm});
            skLineSegment(sketch, "E345", {"start": v(-47.8, 19.7) * mm, "end": v(-47.85, 19.72) * mm});
            skLineSegment(sketch, "E346", {"start": v(-47.85, 19.72) * mm, "end": v(-47.86, 19.72) * mm});
            skSolve(sketch);
        }
        {
            var Q0;
            Q0 = qSketchRegion(id + "F8", true);
            extrude(context, id + "F9", {"entities" : qUnion([Q0]), "depth" : 3.5 * mm, "offsetDistance" : 25 * mm});
        }
        {
            var Q0;
            Q0=qCreatedBy(makeId("Front.planeOp"),FACE);
            var sketch = newSketch(context, id + "F10", { "sketchPlane" : qUnion([Q0])});
            skLineSegment(sketch, "E347", {"start": v(-48, 24.52) * mm, "end": v(-47.93, 24.95) * mm});
            skLineSegment(sketch, "E348", {"start": v(-47.93, 24.95) * mm, "end": v(-47.77, 25.27) * mm});
            skLineSegment(sketch, "E349", {"start": v(-47.77, 25.27) * mm, "end": v(-47.54, 25.67) * mm});
            skLineSegment(sketch, "E350", {"start": v(-47.54, 25.67) * mm, "end": v(-47.35, 26.04) * mm});
            skLineSegment(sketch, "E351", {"start": v(-47.35, 26.04) * mm, "end": v(-47.28, 26.47) * mm});
            skLineSegment(sketch, "E352", {"start": v(-47.28, 26.47) * mm, "end": v(-47.28, 26.91) * mm});
            skLineSegment(sketch, "E353", {"start": v(-47.28, 26.91) * mm, "end": v(-47.28, 27.21) * mm});
            skLineSegment(sketch, "E354", {"start": v(-47.28, 27.21) * mm, "end": v(-47.37, 27.33) * mm});
            skLineSegment(sketch, "E355", {"start": v(-47.37, 27.33) * mm, "end": v(-47.63, 27.13) * mm});
            skLineSegment(sketch, "E356", {"start": v(-47.63, 27.13) * mm, "end": v(-47.79, 26.98) * mm});
            skLineSegment(sketch, "E357", {"start": v(-47.79, 26.98) * mm, "end": v(-48.06, 26.84) * mm});
            skLineSegment(sketch, "E358", {"start": v(-48.06, 26.84) * mm, "end": v(-48.28, 26.84) * mm});
            skLineSegment(sketch, "E359", {"start": v(-48.28, 26.84) * mm, "end": v(-48.38, 26.93) * mm});
            skLineSegment(sketch, "E360", {"start": v(-48.38, 26.93) * mm, "end": v(-48.5, 27.15) * mm});
            skLineSegment(sketch, "E361", {"start": v(-48.5, 27.15) * mm, "end": v(-48.5, 27.34) * mm});
            skLineSegment(sketch, "E362", {"start": v(-48.5, 27.34) * mm, "end": v(-48.7, 27.43) * mm});
            skLineSegment(sketch, "E363", {"start": v(-48.7, 27.43) * mm, "end": v(-48.86, 27.43) * mm});
            skLineSegment(sketch, "E364", {"start": v(-48.86, 27.43) * mm, "end": v(-48.94, 27.58) * mm});
            skLineSegment(sketch, "E365", {"start": v(-48.94, 27.58) * mm, "end": v(-48.94, 27.72) * mm});
            skLineSegment(sketch, "E366", {"start": v(-48.94, 27.72) * mm, "end": v(-48.94, 27.84) * mm});
            skLineSegment(sketch, "E367", {"start": v(-48.94, 27.84) * mm, "end": v(-49.02, 27.84) * mm});
            skLineSegment(sketch, "E368", {"start": v(-49.02, 27.84) * mm, "end": v(-49.15, 27.77) * mm});
            skLineSegment(sketch, "E369", {"start": v(-49.15, 27.77) * mm, "end": v(-49.27, 27.7) * mm});
            skLineSegment(sketch, "E370", {"start": v(-49.27, 27.7) * mm, "end": v(-49.32, 27.74) * mm});
            skLineSegment(sketch, "E371", {"start": v(-49.32, 27.74) * mm, "end": v(-49.35, 27.84) * mm});
            skLineSegment(sketch, "E372", {"start": v(-49.35, 27.84) * mm, "end": v(-49.35, 27.95) * mm});
            skLineSegment(sketch, "E373", {"start": v(-49.35, 27.95) * mm, "end": v(-49.35, 28.04) * mm});
            skLineSegment(sketch, "E374", {"start": v(-49.35, 28.04) * mm, "end": v(-49.46, 28.04) * mm});
            skLineSegment(sketch, "E375", {"start": v(-49.46, 28.04) * mm, "end": v(-49.59, 27.97) * mm});
            skLineSegment(sketch, "E376", {"start": v(-49.59, 27.97) * mm, "end": v(-49.67, 27.97) * mm});
            skLineSegment(sketch, "E377", {"start": v(-49.67, 27.97) * mm, "end": v(-49.77, 27.97) * mm});
            skLineSegment(sketch, "E378", {"start": v(-49.77, 27.97) * mm, "end": v(-49.86, 28.05) * mm});
            skLineSegment(sketch, "E379", {"start": v(-49.86, 28.05) * mm, "end": v(-49.9, 28.12) * mm});
            skLineSegment(sketch, "E380", {"start": v(-49.9, 28.12) * mm, "end": v(-49.9, 28.3) * mm});
            skLineSegment(sketch, "E381", {"start": v(-49.9, 28.3) * mm, "end": v(-49.9, 28.46) * mm});
            skLineSegment(sketch, "E382", {"start": v(-49.9, 28.46) * mm, "end": v(-49.9, 28.6) * mm});
            skLineSegment(sketch, "E383", {"start": v(-49.9, 28.6) * mm, "end": v(-49.9, 28.88) * mm});
            skLineSegment(sketch, "E384", {"start": v(-49.9, 28.88) * mm, "end": v(-49.9, 29.1) * mm});
            skLineSegment(sketch, "E385", {"start": v(-49.9, 29.1) * mm, "end": v(-49.97, 29.18) * mm});
            skLineSegment(sketch, "E386", {"start": v(-49.97, 29.18) * mm, "end": v(-50.06, 29.18) * mm});
            skLineSegment(sketch, "E387", {"start": v(-50.06, 29.18) * mm, "end": v(-50.11, 29.28) * mm});
            skLineSegment(sketch, "E388", {"start": v(-50.11, 29.28) * mm, "end": v(-50.2, 29.43) * mm});
            skLineSegment(sketch, "E389", {"start": v(-50.2, 29.43) * mm, "end": v(-50.2, 29.59) * mm});
            skLineSegment(sketch, "E390", {"start": v(-50.2, 29.59) * mm, "end": v(-50.2, 29.75) * mm});
            skLineSegment(sketch, "E391", {"start": v(-50.2, 29.75) * mm, "end": v(-50.28, 29.82) * mm});
            skLineSegment(sketch, "E392", {"start": v(-50.28, 29.82) * mm, "end": v(-50.38, 30.02) * mm});
            skLineSegment(sketch, "E393", {"start": v(-50.38, 30.02) * mm, "end": v(-50.38, 30.25) * mm});
            skLineSegment(sketch, "E394", {"start": v(-50.38, 30.25) * mm, "end": v(-50.55, 30.4) * mm});
            skLineSegment(sketch, "E395", {"start": v(-50.55, 30.4) * mm, "end": v(-50.75, 30.4) * mm});
            skLineSegment(sketch, "E396", {"start": v(-50.75, 30.4) * mm, "end": v(-50.9, 30.7) * mm});
            skLineSegment(sketch, "E397", {"start": v(-50.9, 30.7) * mm, "end": v(-50.8, 31) * mm});
            skLineSegment(sketch, "E398", {"start": v(-50.8, 31) * mm, "end": v(-50.6, 31.35) * mm});
            skLineSegment(sketch, "E399", {"start": v(-50.6, 31.35) * mm, "end": v(-50.38, 31.59) * mm});
            skLineSegment(sketch, "E400", {"start": v(-50.38, 31.59) * mm, "end": v(-50.2, 31.8) * mm});
            skLineSegment(sketch, "E401", {"start": v(-50.2, 31.8) * mm, "end": v(-49.7, 32.33) * mm});
            skLineSegment(sketch, "E402", {"start": v(-49.7, 32.33) * mm, "end": v(-49.06, 32.67) * mm});
            skLineSegment(sketch, "E403", {"start": v(-49.06, 32.67) * mm, "end": v(-48.68, 32.88) * mm});
            skLineSegment(sketch, "E404", {"start": v(-48.68, 32.88) * mm, "end": v(-48.17, 32.88) * mm});
            skLineSegment(sketch, "E405", {"start": v(-48.17, 32.88) * mm, "end": v(-47.62, 32.88) * mm});
            skLineSegment(sketch, "E406", {"start": v(-47.62, 32.88) * mm, "end": v(-47.22, 32.88) * mm});
            skLineSegment(sketch, "E407", {"start": v(-47.22, 32.88) * mm, "end": v(-46.67, 32.58) * mm});
            skLineSegment(sketch, "E408", {"start": v(-46.67, 32.58) * mm, "end": v(-46.3, 31.88) * mm});
            skLineSegment(sketch, "E409", {"start": v(-46.3, 31.88) * mm, "end": v(-46, 31.32) * mm});
            skLineSegment(sketch, "E410", {"start": v(-46, 31.32) * mm, "end": v(-45.85, 30.76) * mm});
            skLineSegment(sketch, "E411", {"start": v(-45.85, 30.76) * mm, "end": v(-45.66, 30.4) * mm});
            skLineSegment(sketch, "E412", {"start": v(-45.66, 30.4) * mm, "end": v(-45.38, 30.16) * mm});
            skLineSegment(sketch, "E413", {"start": v(-45.38, 30.16) * mm, "end": v(-45.17, 29.75) * mm});
            skLineSegment(sketch, "E414", {"start": v(-45.17, 29.75) * mm, "end": v(-44.68, 29.75) * mm});
            skLineSegment(sketch, "E415", {"start": v(-44.68, 29.75) * mm, "end": v(-43.72, 30.26) * mm});
            skLineSegment(sketch, "E416", {"start": v(-43.72, 30.26) * mm, "end": v(-42.95, 30.85) * mm});
            skLineSegment(sketch, "E417", {"start": v(-42.95, 30.85) * mm, "end": v(-42.53, 31.31) * mm});
            skLineSegment(sketch, "E418", {"start": v(-42.53, 31.31) * mm, "end": v(-41.98, 31.6) * mm});
            skLineSegment(sketch, "E419", {"start": v(-41.98, 31.6) * mm, "end": v(-41.75, 31.4) * mm});
            skLineSegment(sketch, "E420", {"start": v(-41.75, 31.4) * mm, "end": v(-41.44, 31.4) * mm});
            skLineSegment(sketch, "E421", {"start": v(-41.44, 31.4) * mm, "end": v(-41.2, 31.36) * mm});
            skLineSegment(sketch, "E422", {"start": v(-41.2, 31.36) * mm, "end": v(-41.25, 31.13) * mm});
            skLineSegment(sketch, "E423", {"start": v(-41.25, 31.13) * mm, "end": v(-41.31, 30.9) * mm});
            skLineSegment(sketch, "E424", {"start": v(-41.31, 30.9) * mm, "end": v(-41.35, 30.75) * mm});
            skLineSegment(sketch, "E425", {"start": v(-41.35, 30.75) * mm, "end": v(-41.42, 30.56) * mm});
            skLineSegment(sketch, "E426", {"start": v(-41.42, 30.56) * mm, "end": v(-41.5, 30.33) * mm});
            skLineSegment(sketch, "E427", {"start": v(-41.5, 30.33) * mm, "end": v(-41.6, 30.02) * mm});
            skLineSegment(sketch, "E428", {"start": v(-41.6, 30.02) * mm, "end": v(-41.72, 29.72) * mm});
            skLineSegment(sketch, "E429", {"start": v(-41.72, 29.72) * mm, "end": v(-41.85, 29.43) * mm});
            skLineSegment(sketch, "E430", {"start": v(-41.85, 29.43) * mm, "end": v(-41.97, 29.15) * mm});
            skLineSegment(sketch, "E431", {"start": v(-41.97, 29.15) * mm, "end": v(-42.13, 29) * mm});
            skLineSegment(sketch, "E432", {"start": v(-42.13, 29) * mm, "end": v(-42.4, 28.74) * mm});
            skLineSegment(sketch, "E433", {"start": v(-42.4, 28.74) * mm, "end": v(-42.82, 28.35) * mm});
            skLineSegment(sketch, "E434", {"start": v(-42.82, 28.35) * mm, "end": v(-43.07, 28.14) * mm});
            skLineSegment(sketch, "E435", {"start": v(-43.07, 28.14) * mm, "end": v(-43.38, 27.9) * mm});
            skLineSegment(sketch, "E436", {"start": v(-43.38, 27.9) * mm, "end": v(-43.58, 27.74) * mm});
            skLineSegment(sketch, "E437", {"start": v(-43.58, 27.74) * mm, "end": v(-43.8, 27.56) * mm});
            skLineSegment(sketch, "E438", {"start": v(-43.8, 27.56) * mm, "end": v(-44.02, 27.38) * mm});
            skLineSegment(sketch, "E439", {"start": v(-44.02, 27.38) * mm, "end": v(-44.2, 27.28) * mm});
            skLineSegment(sketch, "E440", {"start": v(-44.2, 27.28) * mm, "end": v(-44.6, 27.07) * mm});
            skLineSegment(sketch, "E441", {"start": v(-44.6, 27.07) * mm, "end": v(-45.3, 26.77) * mm});
            skLineSegment(sketch, "E442", {"start": v(-45.3, 26.77) * mm, "end": v(-45.56, 26.63) * mm});
            skLineSegment(sketch, "E443", {"start": v(-45.56, 26.63) * mm, "end": v(-45.94, 26.42) * mm});
            skLineSegment(sketch, "E444", {"start": v(-45.94, 26.42) * mm, "end": v(-46.11, 26.29) * mm});
            skLineSegment(sketch, "E445", {"start": v(-46.11, 26.29) * mm, "end": v(-46.33, 26.09) * mm});
            skLineSegment(sketch, "E446", {"start": v(-46.33, 26.09) * mm, "end": v(-46.83, 25.64) * mm});
            skLineSegment(sketch, "E447", {"start": v(-46.83, 25.64) * mm, "end": v(-47.73, 24.78) * mm});
            skLineSegment(sketch, "E448", {"start": v(-47.73, 24.78) * mm, "end": v(-47.92, 24.62) * mm});
            skLineSegment(sketch, "E449", {"start": v(-47.92, 24.62) * mm, "end": v(-48, 24.52) * mm});
            skSolve(sketch);
        }
        {
            var Q0;
            Q0=makeQuery(id+"F10.imprint","IMPRINT",FACE,{"disambiguationData":[TD([[makeQuery(id+"F10.imprint","IMPRINT",EDGE,{"derivedFrom":sQuery(id+"F10.wireOp",EDGE,"E347")}),-1.0]])]});
            extrude(context, id + "F11", {"entities" : qUnion([Q0]), "operationType" : NewBodyOperationType.ADD, "depth" : 2.5 * mm, "offsetDistance" : 25 * mm});
        }
        {
            var Q0;
            Q0=qCreatedBy(makeId("Front.planeOp"),FACE);
            var sketch = newSketch(context, id + "F12", { "sketchPlane" : qUnion([Q0])});
            skLineSegment(sketch, "E450", {"start": v(-49.46, 8.7) * mm, "end": v(-50.03, 7.9) * mm});
            skLineSegment(sketch, "E451", {"start": v(-50.03, 7.9) * mm, "end": v(-50.28, 7.63) * mm});
            skLineSegment(sketch, "E452", {"start": v(-50.28, 7.63) * mm, "end": v(-50.73, 7.36) * mm});
            skLineSegment(sketch, "E453", {"start": v(-50.73, 7.36) * mm, "end": v(-51.12, 7.08) * mm});
            skLineSegment(sketch, "E454", {"start": v(-51.12, 7.08) * mm, "end": v(-51.41, 6.8) * mm});
            skLineSegment(sketch, "E455", {"start": v(-51.41, 6.8) * mm, "end": v(-51.8, 6.42) * mm});
            skLineSegment(sketch, "E456", {"start": v(-51.8, 6.42) * mm, "end": v(-52.05, 6.05) * mm});
            skLineSegment(sketch, "E457", {"start": v(-52.05, 6.05) * mm, "end": v(-52.42, 5.74) * mm});
            skLineSegment(sketch, "E458", {"start": v(-52.42, 5.74) * mm, "end": v(-52.6, 5.51) * mm});
            skLineSegment(sketch, "E459", {"start": v(-52.6, 5.51) * mm, "end": v(-52.78, 5.44) * mm});
            skLineSegment(sketch, "E460", {"start": v(-52.78, 5.44) * mm, "end": v(-53.02, 5.44) * mm});
            skLineSegment(sketch, "E461", {"start": v(-53.02, 5.44) * mm, "end": v(-53.36, 5.18) * mm});
            skLineSegment(sketch, "E462", {"start": v(-53.36, 5.18) * mm, "end": v(-53.75, 4.77) * mm});
            skLineSegment(sketch, "E463", {"start": v(-53.75, 4.77) * mm, "end": v(-54.2, 4.35) * mm});
            skLineSegment(sketch, "E464", {"start": v(-54.2, 4.35) * mm, "end": v(-54.36, 4.1) * mm});
            skLineSegment(sketch, "E465", {"start": v(-54.36, 4.1) * mm, "end": v(-54.72, 4.02) * mm});
            skLineSegment(sketch, "E466", {"start": v(-54.72, 4.02) * mm, "end": v(-55.16, 3.89) * mm});
            skLineSegment(sketch, "E467", {"start": v(-55.16, 3.89) * mm, "end": v(-55.5, 3.73) * mm});
            skLineSegment(sketch, "E468", {"start": v(-55.5, 3.73) * mm, "end": v(-55.77, 3.55) * mm});
            skLineSegment(sketch, "E469", {"start": v(-55.77, 3.55) * mm, "end": v(-55.92, 3.4) * mm});
            skLineSegment(sketch, "E470", {"start": v(-55.92, 3.4) * mm, "end": v(-55.92, 3.18) * mm});
            skLineSegment(sketch, "E471", {"start": v(-55.92, 3.18) * mm, "end": v(-55.92, 3.03) * mm});
            skLineSegment(sketch, "E472", {"start": v(-55.92, 3.03) * mm, "end": v(-55.69, 2.8) * mm});
            skLineSegment(sketch, "E473", {"start": v(-55.69, 2.8) * mm, "end": v(-55.46, 2.8) * mm});
            skLineSegment(sketch, "E474", {"start": v(-55.46, 2.8) * mm, "end": v(-55.02, 2.75) * mm});
            skLineSegment(sketch, "E475", {"start": v(-55.02, 2.75) * mm, "end": v(-54.78, 2.75) * mm});
            skLineSegment(sketch, "E476", {"start": v(-54.78, 2.75) * mm, "end": v(-54.5, 2.73) * mm});
            skLineSegment(sketch, "E477", {"start": v(-54.5, 2.73) * mm, "end": v(-54.19, 2.74) * mm});
            skLineSegment(sketch, "E478", {"start": v(-54.19, 2.74) * mm, "end": v(-53.9, 2.74) * mm});
            skLineSegment(sketch, "E479", {"start": v(-53.9, 2.74) * mm, "end": v(-53.5, 2.8) * mm});
            skLineSegment(sketch, "E480", {"start": v(-53.5, 2.8) * mm, "end": v(-53.1, 3) * mm});
            skLineSegment(sketch, "E481", {"start": v(-53.1, 3) * mm, "end": v(-52.74, 3.23) * mm});
            skLineSegment(sketch, "E482", {"start": v(-52.74, 3.23) * mm, "end": v(-52.5, 3.36) * mm});
            skLineSegment(sketch, "E483", {"start": v(-52.5, 3.36) * mm, "end": v(-52.22, 3.46) * mm});
            skLineSegment(sketch, "E484", {"start": v(-52.22, 3.46) * mm, "end": v(-52, 3.46) * mm});
            skLineSegment(sketch, "E485", {"start": v(-52, 3.46) * mm, "end": v(-51.86, 3.5) * mm});
            skLineSegment(sketch, "E486", {"start": v(-51.86, 3.5) * mm, "end": v(-51.86, 3.1) * mm});
            skLineSegment(sketch, "E487", {"start": v(-51.86, 3.1) * mm, "end": v(-51.83, 3) * mm});
            skLineSegment(sketch, "E488", {"start": v(-51.83, 3) * mm, "end": v(-51.42, 3) * mm});
            skLineSegment(sketch, "E489", {"start": v(-51.42, 3) * mm, "end": v(-50.8, 3) * mm});
            skLineSegment(sketch, "E490", {"start": v(-50.8, 3) * mm, "end": v(-50.43, 3) * mm});
            skLineSegment(sketch, "E491", {"start": v(-50.43, 3) * mm, "end": v(-50.37, 3.14) * mm});
            skLineSegment(sketch, "E492", {"start": v(-50.37, 3.14) * mm, "end": v(-50.37, 3.36) * mm});
            skLineSegment(sketch, "E493", {"start": v(-50.37, 3.36) * mm, "end": v(-50.37, 3.55) * mm});
            skLineSegment(sketch, "E494", {"start": v(-50.37, 3.55) * mm, "end": v(-50.32, 3.73) * mm});
            skLineSegment(sketch, "E495", {"start": v(-50.32, 3.73) * mm, "end": v(-50.21, 3.8) * mm});
            skLineSegment(sketch, "E496", {"start": v(-50.21, 3.8) * mm, "end": v(-49.63, 3.23) * mm});
            skLineSegment(sketch, "E497", {"start": v(-49.63, 3.23) * mm, "end": v(-49.24, 2.85) * mm});
            skLineSegment(sketch, "E498", {"start": v(-49.24, 2.85) * mm, "end": v(-49.11, 2.78) * mm});
            skLineSegment(sketch, "E499", {"start": v(-49.11, 2.78) * mm, "end": v(-48.59, 3.32) * mm});
            skLineSegment(sketch, "E500", {"start": v(-48.59, 3.32) * mm, "end": v(-48.08, 3.93) * mm});
            skLineSegment(sketch, "E501", {"start": v(-48.08, 3.93) * mm, "end": v(-47.67, 4.36) * mm});
            skLineSegment(sketch, "E502", {"start": v(-47.67, 4.36) * mm, "end": v(-47.02, 5.12) * mm});
            skLineSegment(sketch, "E503", {"start": v(-47.02, 5.12) * mm, "end": v(-46.36, 5.93) * mm});
            skLineSegment(sketch, "E504", {"start": v(-46.36, 5.93) * mm, "end": v(-45.7, 6.6) * mm});
            skLineSegment(sketch, "E505", {"start": v(-45.7, 6.6) * mm, "end": v(-45.33, 6.99) * mm});
            skLineSegment(sketch, "E506", {"start": v(-45.33, 6.99) * mm, "end": v(-44.62, 7.7) * mm});
            skLineSegment(sketch, "E507", {"start": v(-44.62, 7.7) * mm, "end": v(-44.5, 8) * mm});
            skLineSegment(sketch, "E508", {"start": v(-44.5, 8) * mm, "end": v(-44.96, 7.9) * mm});
            skLineSegment(sketch, "E509", {"start": v(-44.96, 7.9) * mm, "end": v(-45.45, 7.9) * mm});
            skLineSegment(sketch, "E510", {"start": v(-45.45, 7.9) * mm, "end": v(-46.13, 7.9) * mm});
            skLineSegment(sketch, "E511", {"start": v(-46.13, 7.9) * mm, "end": v(-46.75, 7.9) * mm});
            skLineSegment(sketch, "E512", {"start": v(-46.75, 7.9) * mm, "end": v(-47.28, 8.09) * mm});
            skLineSegment(sketch, "E513", {"start": v(-47.28, 8.09) * mm, "end": v(-47.58, 8.34) * mm});
            skLineSegment(sketch, "E514", {"start": v(-47.58, 8.34) * mm, "end": v(-48.08, 8.67) * mm});
            skLineSegment(sketch, "E515", {"start": v(-48.08, 8.67) * mm, "end": v(-48.28, 8.98) * mm});
            skLineSegment(sketch, "E516", {"start": v(-48.28, 8.98) * mm, "end": v(-48.5, 9.2) * mm});
            skLineSegment(sketch, "E517", {"start": v(-48.5, 9.2) * mm, "end": v(-48.67, 9.14) * mm});
            skLineSegment(sketch, "E518", {"start": v(-48.67, 9.14) * mm, "end": v(-48.92, 8.98) * mm});
            skLineSegment(sketch, "E519", {"start": v(-48.92, 8.98) * mm, "end": v(-49.2, 8.85) * mm});
            skLineSegment(sketch, "E520", {"start": v(-49.2, 8.85) * mm, "end": v(-49.35, 8.75) * mm});
            skLineSegment(sketch, "E521", {"start": v(-49.35, 8.75) * mm, "end": v(-49.46, 8.7) * mm});
            skSolve(sketch);
        }
        {
            var Q0;
            Q0 = qSketchRegion(id + "F12", true);
            extrude(context, id + "F13", {"entities" : qUnion([Q0]), "operationType" : NewBodyOperationType.ADD, "depth" : 2.5 * mm, "offsetDistance" : 25 * mm});
        }
        {
            var Q0;
            Q0=qCreatedBy(makeId("Front.planeOp"),FACE);
            var sketch = newSketch(context, id + "F14", { "sketchPlane" : qUnion([Q0])});
            skLineSegment(sketch, "E522", {"start": v(-35.58, 16.49) * mm, "end": v(-36.23, 16.14) * mm});
            skLineSegment(sketch, "E523", {"start": v(-36.23, 16.14) * mm, "end": v(-37.04, 15.72) * mm});
            skLineSegment(sketch, "E524", {"start": v(-37.04, 15.72) * mm, "end": v(-37.88, 15.39) * mm});
            skLineSegment(sketch, "E525", {"start": v(-37.88, 15.39) * mm, "end": v(-38.8, 15.11) * mm});
            skLineSegment(sketch, "E526", {"start": v(-38.8, 15.11) * mm, "end": v(-39.49, 15) * mm});
            skLineSegment(sketch, "E527", {"start": v(-39.49, 15) * mm, "end": v(-39.84, 15) * mm});
            skLineSegment(sketch, "E528", {"start": v(-39.84, 15) * mm, "end": v(-39.92, 14.8) * mm});
            skLineSegment(sketch, "E529", {"start": v(-39.92, 14.8) * mm, "end": v(-40.04, 14.53) * mm});
            skLineSegment(sketch, "E530", {"start": v(-40.04, 14.53) * mm, "end": v(-40.23, 14.13) * mm});
            skLineSegment(sketch, "E531", {"start": v(-40.23, 14.13) * mm, "end": v(-40.31, 13.95) * mm});
            skLineSegment(sketch, "E532", {"start": v(-40.31, 13.95) * mm, "end": v(-40.35, 13.87) * mm});
            skLineSegment(sketch, "E533", {"start": v(-40.35, 13.87) * mm, "end": v(-40.4, 13.65) * mm});
            skLineSegment(sketch, "E534", {"start": v(-40.4, 13.65) * mm, "end": v(-40.47, 13.31) * mm});
            skLineSegment(sketch, "E535", {"start": v(-40.47, 13.31) * mm, "end": v(-40.53, 13) * mm});
            skLineSegment(sketch, "E536", {"start": v(-40.53, 13) * mm, "end": v(-40.6, 12.72) * mm});
            skLineSegment(sketch, "E537", {"start": v(-40.6, 12.72) * mm, "end": v(-40.63, 12.5) * mm});
            skLineSegment(sketch, "E538", {"start": v(-40.63, 12.5) * mm, "end": v(-40.67, 12.3) * mm});
            skLineSegment(sketch, "E539", {"start": v(-40.67, 12.3) * mm, "end": v(-40.68, 12.27) * mm});
            skLineSegment(sketch, "E540", {"start": v(-40.68, 12.27) * mm, "end": v(-40.68, 12.24) * mm});
            skLineSegment(sketch, "E541", {"start": v(-40.68, 12.24) * mm, "end": v(-40.67, 12.04) * mm});
            skLineSegment(sketch, "E542", {"start": v(-40.67, 12.04) * mm, "end": v(-40.68, 11.9) * mm});
            skLineSegment(sketch, "E543", {"start": v(-40.68, 11.9) * mm, "end": v(-40.68, 11.71) * mm});
            skLineSegment(sketch, "E544", {"start": v(-40.68, 11.71) * mm, "end": v(-40.68, 11.54) * mm});
            skLineSegment(sketch, "E545", {"start": v(-40.68, 11.54) * mm, "end": v(-40.68, 11.37) * mm});
            skLineSegment(sketch, "E546", {"start": v(-40.68, 11.37) * mm, "end": v(-40.68, 10.98) * mm});
            skLineSegment(sketch, "E547", {"start": v(-40.68, 10.98) * mm, "end": v(-40.68, 10.84) * mm});
            skLineSegment(sketch, "E548", {"start": v(-40.68, 10.84) * mm, "end": v(-40.7, 10.75) * mm});
            skLineSegment(sketch, "E549", {"start": v(-40.7, 10.75) * mm, "end": v(-40.76, 10.56) * mm});
            skLineSegment(sketch, "E550", {"start": v(-40.76, 10.56) * mm, "end": v(-40.83, 10.24) * mm});
            skLineSegment(sketch, "E551", {"start": v(-40.83, 10.24) * mm, "end": v(-40.91, 10) * mm});
            skLineSegment(sketch, "E552", {"start": v(-40.91, 10) * mm, "end": v(-41, 9.48) * mm});
            skLineSegment(sketch, "E553", {"start": v(-41, 9.48) * mm, "end": v(-41.04, 9.31) * mm});
            skLineSegment(sketch, "E554", {"start": v(-41.04, 9.31) * mm, "end": v(-40.95, 9.04) * mm});
            skLineSegment(sketch, "E555", {"start": v(-40.95, 9.04) * mm, "end": v(-40.88, 8.78) * mm});
            skLineSegment(sketch, "E556", {"start": v(-40.88, 8.78) * mm, "end": v(-40.81, 8.4) * mm});
            skLineSegment(sketch, "E557", {"start": v(-40.81, 8.4) * mm, "end": v(-40.67, 8.05) * mm});
            skLineSegment(sketch, "E558", {"start": v(-40.67, 8.05) * mm, "end": v(-40.4, 7.75) * mm});
            skLineSegment(sketch, "E559", {"start": v(-40.4, 7.75) * mm, "end": v(-40.14, 7.63) * mm});
            skLineSegment(sketch, "E560", {"start": v(-40.14, 7.63) * mm, "end": v(-40.35, 7) * mm});
            skLineSegment(sketch, "E561", {"start": v(-40.35, 7) * mm, "end": v(-40.35, 6.62) * mm});
            skLineSegment(sketch, "E562", {"start": v(-40.35, 6.62) * mm, "end": v(-40.3, 5.93) * mm});
            skLineSegment(sketch, "E563", {"start": v(-40.3, 5.93) * mm, "end": v(-40.3, 5.17) * mm});
            skLineSegment(sketch, "E564", {"start": v(-40.3, 5.17) * mm, "end": v(-40.35, 4.54) * mm});
            skLineSegment(sketch, "E565", {"start": v(-40.35, 4.54) * mm, "end": v(-40.35, 4.07) * mm});
            skLineSegment(sketch, "E566", {"start": v(-40.35, 4.07) * mm, "end": v(-40.35, 3.32) * mm});
            skLineSegment(sketch, "E567", {"start": v(-40.35, 3.32) * mm, "end": v(-40.35, 2.83) * mm});
            skLineSegment(sketch, "E568", {"start": v(-40.35, 2.83) * mm, "end": v(-40.6, 2.28) * mm});
            skLineSegment(sketch, "E569", {"start": v(-40.6, 2.28) * mm, "end": v(-40.88, 1.66) * mm});
            skLineSegment(sketch, "E570", {"start": v(-40.88, 1.66) * mm, "end": v(-40.88, 0.87) * mm});
            skLineSegment(sketch, "E571", {"start": v(-40.88, 0.87) * mm, "end": v(-40.6, 0.54) * mm});
            skLineSegment(sketch, "E572", {"start": v(-40.6, 0.54) * mm, "end": v(-39.84, 0.37) * mm});
            skLineSegment(sketch, "E573", {"start": v(-39.84, 0.37) * mm, "end": v(-38.62, 0.76) * mm});
            skLineSegment(sketch, "E574", {"start": v(-38.62, 0.76) * mm, "end": v(-38.45, 1.1) * mm});
            skLineSegment(sketch, "E575", {"start": v(-38.45, 1.1) * mm, "end": v(-38.33, 1.65) * mm});
            skLineSegment(sketch, "E576", {"start": v(-38.33, 1.65) * mm, "end": v(-38.19, 2.3) * mm});
            skLineSegment(sketch, "E577", {"start": v(-38.19, 2.3) * mm, "end": v(-38.19, 2.83) * mm});
            skLineSegment(sketch, "E578", {"start": v(-38.19, 2.83) * mm, "end": v(-38.19, 3.33) * mm});
            skLineSegment(sketch, "E579", {"start": v(-38.19, 3.33) * mm, "end": v(-38.19, 3.55) * mm});
            skLineSegment(sketch, "E580", {"start": v(-38.19, 3.55) * mm, "end": v(-38.08, 4.04) * mm});
            skLineSegment(sketch, "E581", {"start": v(-38.08, 4.04) * mm, "end": v(-37.98, 4.72) * mm});
            skLineSegment(sketch, "E582", {"start": v(-37.98, 4.72) * mm, "end": v(-37.87, 5.16) * mm});
            skLineSegment(sketch, "E583", {"start": v(-37.87, 5.16) * mm, "end": v(-37.7, 5.55) * mm});
            skLineSegment(sketch, "E584", {"start": v(-37.7, 5.55) * mm, "end": v(-37.7, 5.93) * mm});
            skLineSegment(sketch, "E585", {"start": v(-37.7, 5.93) * mm, "end": v(-37.8, 6.26) * mm});
            skLineSegment(sketch, "E586", {"start": v(-37.8, 6.26) * mm, "end": v(-37.78, 6.52) * mm});
            skLineSegment(sketch, "E587", {"start": v(-37.78, 6.52) * mm, "end": v(-37.7, 6.73) * mm});
            skLineSegment(sketch, "E588", {"start": v(-37.7, 6.73) * mm, "end": v(-37.63, 7) * mm});
            skLineSegment(sketch, "E589", {"start": v(-37.63, 7) * mm, "end": v(-37.57, 7.1) * mm});
            skLineSegment(sketch, "E590", {"start": v(-37.57, 7.1) * mm, "end": v(-37.37, 7.4) * mm});
            skLineSegment(sketch, "E591", {"start": v(-37.37, 7.4) * mm, "end": v(-37.32, 7.48) * mm});
            skLineSegment(sketch, "E592", {"start": v(-37.32, 7.48) * mm, "end": v(-37.32, 7.63) * mm});
            skLineSegment(sketch, "E593", {"start": v(-37.32, 7.63) * mm, "end": v(-37.32, 7.73) * mm});
            skLineSegment(sketch, "E594", {"start": v(-37.32, 7.73) * mm, "end": v(-37.32, 7.95) * mm});
            skLineSegment(sketch, "E595", {"start": v(-37.32, 7.95) * mm, "end": v(-37.32, 8.1) * mm});
            skLineSegment(sketch, "E596", {"start": v(-37.32, 8.1) * mm, "end": v(-37.32, 8.2) * mm});
            skLineSegment(sketch, "E597", {"start": v(-37.32, 8.2) * mm, "end": v(-37.32, 8.4) * mm});
            skLineSegment(sketch, "E598", {"start": v(-37.32, 8.4) * mm, "end": v(-37.32, 8.48) * mm});
            skLineSegment(sketch, "E599", {"start": v(-37.32, 8.48) * mm, "end": v(-37.27, 8.6) * mm});
            skLineSegment(sketch, "E600", {"start": v(-37.27, 8.6) * mm, "end": v(-37.22, 8.7) * mm});
            skLineSegment(sketch, "E601", {"start": v(-37.22, 8.7) * mm, "end": v(-37.14, 8.88) * mm});
            skLineSegment(sketch, "E602", {"start": v(-37.14, 8.88) * mm, "end": v(-37.1, 9.02) * mm});
            skLineSegment(sketch, "E603", {"start": v(-37.1, 9.02) * mm, "end": v(-37.07, 9.2) * mm});
            skLineSegment(sketch, "E604", {"start": v(-37.07, 9.2) * mm, "end": v(-37, 9.38) * mm});
            skLineSegment(sketch, "E605", {"start": v(-37, 9.38) * mm, "end": v(-36.92, 9.57) * mm});
            skLineSegment(sketch, "E606", {"start": v(-36.92, 9.57) * mm, "end": v(-36.87, 9.69) * mm});
            skLineSegment(sketch, "E607", {"start": v(-36.87, 9.69) * mm, "end": v(-36.87, 9.83) * mm});
            skLineSegment(sketch, "E608", {"start": v(-36.87, 9.83) * mm, "end": v(-36.86, 9.91) * mm});
            skLineSegment(sketch, "E609", {"start": v(-36.86, 9.91) * mm, "end": v(-36.64, 10.06) * mm});
            skLineSegment(sketch, "E610", {"start": v(-36.64, 10.06) * mm, "end": v(-36.55, 10.16) * mm});
            skLineSegment(sketch, "E611", {"start": v(-36.55, 10.16) * mm, "end": v(-36.43, 10.3) * mm});
            skLineSegment(sketch, "E612", {"start": v(-36.43, 10.3) * mm, "end": v(-36.34, 10.45) * mm});
            skLineSegment(sketch, "E613", {"start": v(-36.34, 10.45) * mm, "end": v(-36.07, 10.9) * mm});
            skLineSegment(sketch, "E614", {"start": v(-36.07, 10.9) * mm, "end": v(-36, 11.03) * mm});
            skLineSegment(sketch, "E615", {"start": v(-36, 11.03) * mm, "end": v(-35.94, 11.33) * mm});
            skLineSegment(sketch, "E616", {"start": v(-35.94, 11.33) * mm, "end": v(-35.9, 11.55) * mm});
            skLineSegment(sketch, "E617", {"start": v(-35.9, 11.55) * mm, "end": v(-35.8, 11.76) * mm});
            skLineSegment(sketch, "E618", {"start": v(-35.8, 11.76) * mm, "end": v(-35.71, 11.95) * mm});
            skLineSegment(sketch, "E619", {"start": v(-35.71, 11.95) * mm, "end": v(-35.67, 12.1) * mm});
            skLineSegment(sketch, "E620", {"start": v(-35.67, 12.1) * mm, "end": v(-35.5, 12.24) * mm});
            skLineSegment(sketch, "E621", {"start": v(-35.5, 12.24) * mm, "end": v(-35.5, 12.9) * mm});
            skLineSegment(sketch, "E622", {"start": v(-35.5, 12.9) * mm, "end": v(-35.5, 13.5) * mm});
            skLineSegment(sketch, "E623", {"start": v(-35.5, 13.5) * mm, "end": v(-35.44, 14.17) * mm});
            skLineSegment(sketch, "E624", {"start": v(-35.44, 14.17) * mm, "end": v(-35.51, 15) * mm});
            skLineSegment(sketch, "E625", {"start": v(-35.51, 15) * mm, "end": v(-35.51, 15.41) * mm});
            skLineSegment(sketch, "E626", {"start": v(-35.51, 15.41) * mm, "end": v(-35.57, 16.3) * mm});
            skLineSegment(sketch, "E627", {"start": v(-35.57, 16.3) * mm, "end": v(-35.56, 16.34) * mm});
            skLineSegment(sketch, "E628", {"start": v(-35.56, 16.34) * mm, "end": v(-35.58, 16.49) * mm});
            skSolve(sketch);
        }
        {
            var Q0;
            Q0=makeQuery(id+"F14.imprint","IMPRINT",FACE,{"disambiguationData":[TD([[makeQuery(id+"F14.imprint","IMPRINT",EDGE,{"derivedFrom":sQuery(id+"F14.wireOp",EDGE,"E522")}),1.0]])]});
            extrude(context, id + "F15", {"entities" : qUnion([Q0]), "depth" : 3.5 * mm, "offsetDistance" : 25 * mm});
        }
        {
            var Q0;
            Q0=qCreatedBy(makeId("Front.planeOp"),FACE);
            var sketch = newSketch(context, id + "F16", { "sketchPlane" : qUnion([Q0])});
            skLineSegment(sketch, "E629", {"start": v(-35.61, 16.45) * mm, "end": v(-35.21, 16.68) * mm});
            skLineSegment(sketch, "E630", {"start": v(-35.21, 16.68) * mm, "end": v(-34.67, 17) * mm});
            skLineSegment(sketch, "E631", {"start": v(-34.67, 17) * mm, "end": v(-34.26, 17.27) * mm});
            skLineSegment(sketch, "E632", {"start": v(-34.26, 17.27) * mm, "end": v(-33.95, 17.54) * mm});
            skLineSegment(sketch, "E633", {"start": v(-33.95, 17.54) * mm, "end": v(-34.03, 17.78) * mm});
            skLineSegment(sketch, "E634", {"start": v(-34.03, 17.78) * mm, "end": v(-34.2, 18.08) * mm});
            skLineSegment(sketch, "E635", {"start": v(-34.2, 18.08) * mm, "end": v(-34.32, 18.46) * mm});
            skLineSegment(sketch, "E636", {"start": v(-34.32, 18.46) * mm, "end": v(-34.38, 18.76) * mm});
            skLineSegment(sketch, "E637", {"start": v(-34.38, 18.76) * mm, "end": v(-34.6, 19.37) * mm});
            skLineSegment(sketch, "E638", {"start": v(-34.6, 19.37) * mm, "end": v(-34.76, 20.27) * mm});
            skLineSegment(sketch, "E639", {"start": v(-34.76, 20.27) * mm, "end": v(-34.99, 21.01) * mm});
            skLineSegment(sketch, "E640", {"start": v(-34.99, 21.01) * mm, "end": v(-35.17, 21.6) * mm});
            skLineSegment(sketch, "E641", {"start": v(-35.17, 21.6) * mm, "end": v(-35.57, 22.3) * mm});
            skLineSegment(sketch, "E642", {"start": v(-35.57, 22.3) * mm, "end": v(-35.96, 22.68) * mm});
            skLineSegment(sketch, "E643", {"start": v(-35.96, 22.68) * mm, "end": v(-36.55, 23.2) * mm});
            skLineSegment(sketch, "E644", {"start": v(-36.55, 23.2) * mm, "end": v(-37.04, 24.06) * mm});
            skLineSegment(sketch, "E645", {"start": v(-37.04, 24.06) * mm, "end": v(-37.56, 25.08) * mm});
            skLineSegment(sketch, "E646", {"start": v(-37.56, 25.08) * mm, "end": v(-38.19, 26.2) * mm});
            skLineSegment(sketch, "E647", {"start": v(-38.19, 26.2) * mm, "end": v(-38.68, 27.37) * mm});
            skLineSegment(sketch, "E648", {"start": v(-38.68, 27.37) * mm, "end": v(-38.9, 28.11) * mm});
            skLineSegment(sketch, "E649", {"start": v(-38.9, 28.11) * mm, "end": v(-39.04, 28.54) * mm});
            skLineSegment(sketch, "E650", {"start": v(-39.04, 28.54) * mm, "end": v(-38, 28.97) * mm});
            skLineSegment(sketch, "E651", {"start": v(-38, 28.97) * mm, "end": v(-37.4, 29.27) * mm});
            skLineSegment(sketch, "E652", {"start": v(-37.4, 29.27) * mm, "end": v(-36.87, 29.65) * mm});
            skLineSegment(sketch, "E653", {"start": v(-36.87, 29.65) * mm, "end": v(-36.3, 30.18) * mm});
            skLineSegment(sketch, "E654", {"start": v(-36.3, 30.18) * mm, "end": v(-35.93, 30.51) * mm});
            skLineSegment(sketch, "E655", {"start": v(-35.93, 30.51) * mm, "end": v(-35.45, 31.01) * mm});
            skLineSegment(sketch, "E656", {"start": v(-35.45, 31.01) * mm, "end": v(-35.16, 31.4) * mm});
            skLineSegment(sketch, "E657", {"start": v(-35.16, 31.4) * mm, "end": v(-35.1, 31.67) * mm});
            skLineSegment(sketch, "E658", {"start": v(-35.1, 31.67) * mm, "end": v(-35.15, 31.94) * mm});
            skLineSegment(sketch, "E659", {"start": v(-35.15, 31.94) * mm, "end": v(-35.22, 32.17) * mm});
            skLineSegment(sketch, "E660", {"start": v(-35.22, 32.17) * mm, "end": v(-35.4, 32.43) * mm});
            skLineSegment(sketch, "E661", {"start": v(-35.4, 32.43) * mm, "end": v(-35.68, 32.72) * mm});
            skLineSegment(sketch, "E662", {"start": v(-35.68, 32.72) * mm, "end": v(-36.04, 33.15) * mm});
            skLineSegment(sketch, "E663", {"start": v(-36.04, 33.15) * mm, "end": v(-36.44, 33.5) * mm});
            skLineSegment(sketch, "E664", {"start": v(-36.44, 33.5) * mm, "end": v(-36.85, 33.87) * mm});
            skLineSegment(sketch, "E665", {"start": v(-36.85, 33.87) * mm, "end": v(-37.27, 34.23) * mm});
            skLineSegment(sketch, "E666", {"start": v(-37.27, 34.23) * mm, "end": v(-37.74, 34.65) * mm});
            skLineSegment(sketch, "E667", {"start": v(-37.74, 34.65) * mm, "end": v(-38.39, 35) * mm});
            skLineSegment(sketch, "E668", {"start": v(-38.39, 35) * mm, "end": v(-38.88, 35.33) * mm});
            skLineSegment(sketch, "E669", {"start": v(-38.88, 35.33) * mm, "end": v(-39.16, 35.46) * mm});
            skLineSegment(sketch, "E670", {"start": v(-39.16, 35.46) * mm, "end": v(-39.26, 35.6) * mm});
            skLineSegment(sketch, "E671", {"start": v(-39.26, 35.6) * mm, "end": v(-39.38, 35.67) * mm});
            skLineSegment(sketch, "E672", {"start": v(-39.38, 35.67) * mm, "end": v(-39.54, 35.7) * mm});
            skLineSegment(sketch, "E673", {"start": v(-39.54, 35.7) * mm, "end": v(-39.74, 35.7) * mm});
            skLineSegment(sketch, "E674", {"start": v(-39.74, 35.7) * mm, "end": v(-39.92, 35.76) * mm});
            skLineSegment(sketch, "E675", {"start": v(-39.92, 35.76) * mm, "end": v(-40.16, 35.91) * mm});
            skLineSegment(sketch, "E676", {"start": v(-40.16, 35.91) * mm, "end": v(-40.4, 36.03) * mm});
            skLineSegment(sketch, "E677", {"start": v(-40.4, 36.03) * mm, "end": v(-40.7, 36.22) * mm});
            skLineSegment(sketch, "E678", {"start": v(-40.7, 36.22) * mm, "end": v(-41.04, 36.41) * mm});
            skLineSegment(sketch, "E679", {"start": v(-41.04, 36.41) * mm, "end": v(-41.26, 36.61) * mm});
            skLineSegment(sketch, "E680", {"start": v(-41.26, 36.61) * mm, "end": v(-41.4, 36.7) * mm});
            skLineSegment(sketch, "E681", {"start": v(-41.4, 36.7) * mm, "end": v(-41.58, 36.76) * mm});
            skLineSegment(sketch, "E682", {"start": v(-41.58, 36.76) * mm, "end": v(-41.76, 36.73) * mm});
            skLineSegment(sketch, "E683", {"start": v(-41.76, 36.73) * mm, "end": v(-41.97, 36.6) * mm});
            skLineSegment(sketch, "E684", {"start": v(-41.97, 36.6) * mm, "end": v(-42.25, 36.4) * mm});
            skLineSegment(sketch, "E685", {"start": v(-42.25, 36.4) * mm, "end": v(-42.56, 36.2) * mm});
            skLineSegment(sketch, "E686", {"start": v(-42.56, 36.2) * mm, "end": v(-42.76, 35.97) * mm});
            skLineSegment(sketch, "E687", {"start": v(-42.76, 35.97) * mm, "end": v(-42.87, 35.8) * mm});
            skLineSegment(sketch, "E688", {"start": v(-42.87, 35.8) * mm, "end": v(-42.97, 35.58) * mm});
            skLineSegment(sketch, "E689", {"start": v(-42.97, 35.58) * mm, "end": v(-43.04, 35.28) * mm});
            skLineSegment(sketch, "E690", {"start": v(-43.04, 35.28) * mm, "end": v(-43.04, 35) * mm});
            skLineSegment(sketch, "E691", {"start": v(-43.04, 35) * mm, "end": v(-42.94, 34.88) * mm});
            skLineSegment(sketch, "E692", {"start": v(-42.94, 34.88) * mm, "end": v(-42.74, 34.88) * mm});
            skLineSegment(sketch, "E693", {"start": v(-42.74, 34.88) * mm, "end": v(-42.62, 35) * mm});
            skLineSegment(sketch, "E694", {"start": v(-42.62, 35) * mm, "end": v(-42.6, 35.15) * mm});
            skLineSegment(sketch, "E695", {"start": v(-42.6, 35.15) * mm, "end": v(-42.53, 35.48) * mm});
            skLineSegment(sketch, "E696", {"start": v(-42.53, 35.48) * mm, "end": v(-42.5, 35.53) * mm});
            skLineSegment(sketch, "E697", {"start": v(-42.5, 35.53) * mm, "end": v(-42.42, 35.48) * mm});
            skLineSegment(sketch, "E698", {"start": v(-42.42, 35.48) * mm, "end": v(-42.53, 35.3) * mm});
            skLineSegment(sketch, "E699", {"start": v(-42.53, 35.3) * mm, "end": v(-42.48, 35.13) * mm});
            skLineSegment(sketch, "E700", {"start": v(-42.48, 35.13) * mm, "end": v(-42.4, 35) * mm});
            skLineSegment(sketch, "E701", {"start": v(-42.4, 35) * mm, "end": v(-42.35, 34.84) * mm});
            skLineSegment(sketch, "E702", {"start": v(-42.35, 34.84) * mm, "end": v(-42.27, 34.72) * mm});
            skLineSegment(sketch, "E703", {"start": v(-42.27, 34.72) * mm, "end": v(-42.24, 34.61) * mm});
            skLineSegment(sketch, "E704", {"start": v(-42.24, 34.61) * mm, "end": v(-42.04, 34.67) * mm});
            skLineSegment(sketch, "E705", {"start": v(-42.04, 34.67) * mm, "end": v(-41.95, 34.61) * mm});
            skLineSegment(sketch, "E706", {"start": v(-41.95, 34.61) * mm, "end": v(-41.8, 34.52) * mm});
            skLineSegment(sketch, "E707", {"start": v(-41.8, 34.52) * mm, "end": v(-41.73, 34.39) * mm});
            skLineSegment(sketch, "E708", {"start": v(-41.73, 34.39) * mm, "end": v(-41.6, 34.3) * mm});
            skLineSegment(sketch, "E709", {"start": v(-41.6, 34.3) * mm, "end": v(-41.44, 34.28) * mm});
            skLineSegment(sketch, "E710", {"start": v(-41.44, 34.28) * mm, "end": v(-41.4, 34.17) * mm});
            skLineSegment(sketch, "E711", {"start": v(-41.4, 34.17) * mm, "end": v(-41.27, 34.14) * mm});
            skLineSegment(sketch, "E712", {"start": v(-41.27, 34.14) * mm, "end": v(-41.16, 34.22) * mm});
            skLineSegment(sketch, "E713", {"start": v(-41.16, 34.22) * mm, "end": v(-41.1, 34.32) * mm});
            skLineSegment(sketch, "E714", {"start": v(-41.1, 34.32) * mm, "end": v(-41.1, 34.42) * mm});
            skLineSegment(sketch, "E715", {"start": v(-41.1, 34.42) * mm, "end": v(-41.05, 34.5) * mm});
            skLineSegment(sketch, "E716", {"start": v(-41.05, 34.5) * mm, "end": v(-41.14, 34.78) * mm});
            skLineSegment(sketch, "E717", {"start": v(-41.14, 34.78) * mm, "end": v(-40.8, 34.6) * mm});
            skLineSegment(sketch, "E718", {"start": v(-40.8, 34.6) * mm, "end": v(-40.63, 34.57) * mm});
            skLineSegment(sketch, "E719", {"start": v(-40.63, 34.57) * mm, "end": v(-40.08, 34.53) * mm});
            skLineSegment(sketch, "E720", {"start": v(-40.08, 34.53) * mm, "end": v(-39.91, 34.32) * mm});
            skLineSegment(sketch, "E721", {"start": v(-39.91, 34.32) * mm, "end": v(-39.91, 33.79) * mm});
            skLineSegment(sketch, "E722", {"start": v(-39.91, 33.79) * mm, "end": v(-39.78, 33.7) * mm});
            skLineSegment(sketch, "E723", {"start": v(-39.78, 33.7) * mm, "end": v(-39.6, 33.61) * mm});
            skLineSegment(sketch, "E724", {"start": v(-39.6, 33.61) * mm, "end": v(-39.43, 33.5) * mm});
            skLineSegment(sketch, "E725", {"start": v(-39.43, 33.5) * mm, "end": v(-39.25, 33.33) * mm});
            skLineSegment(sketch, "E726", {"start": v(-39.25, 33.33) * mm, "end": v(-39.2, 33.16) * mm});
            skLineSegment(sketch, "E727", {"start": v(-39.2, 33.16) * mm, "end": v(-38.9, 33.14) * mm});
            skLineSegment(sketch, "E728", {"start": v(-38.9, 33.14) * mm, "end": v(-38.83, 32.83) * mm});
            skLineSegment(sketch, "E729", {"start": v(-38.83, 32.83) * mm, "end": v(-38.69, 32.6) * mm});
            skLineSegment(sketch, "E730", {"start": v(-38.69, 32.6) * mm, "end": v(-38.53, 32.35) * mm});
            skLineSegment(sketch, "E731", {"start": v(-38.53, 32.35) * mm, "end": v(-38.47, 32.12) * mm});
            skLineSegment(sketch, "E732", {"start": v(-38.47, 32.12) * mm, "end": v(-38.43, 31.9) * mm});
            skLineSegment(sketch, "E733", {"start": v(-38.43, 31.9) * mm, "end": v(-38.54, 31.74) * mm});
            skLineSegment(sketch, "E734", {"start": v(-38.54, 31.74) * mm, "end": v(-38.74, 31.6) * mm});
            skLineSegment(sketch, "E735", {"start": v(-38.74, 31.6) * mm, "end": v(-38.94, 31.46) * mm});
            skLineSegment(sketch, "E736", {"start": v(-38.94, 31.46) * mm, "end": v(-39.17, 31.38) * mm});
            skLineSegment(sketch, "E737", {"start": v(-39.17, 31.38) * mm, "end": v(-39.54, 31.38) * mm});
            skLineSegment(sketch, "E738", {"start": v(-39.54, 31.38) * mm, "end": v(-39.79, 31.37) * mm});
            skLineSegment(sketch, "E739", {"start": v(-39.79, 31.37) * mm, "end": v(-39.94, 31.37) * mm});
            skLineSegment(sketch, "E740", {"start": v(-39.94, 31.37) * mm, "end": v(-40.05, 31.37) * mm});
            skLineSegment(sketch, "E741", {"start": v(-40.05, 31.37) * mm, "end": v(-40.35, 28.88) * mm});
            skLineSegment(sketch, "E742", {"start": v(-40.35, 28.88) * mm, "end": v(-43.7, 25.46) * mm});
            skLineSegment(sketch, "E743", {"start": v(-43.7, 25.46) * mm, "end": v(-44.57, 24.7) * mm});
            skLineSegment(sketch, "E744", {"start": v(-44.57, 24.7) * mm, "end": v(-44.23, 24.31) * mm});
            skLineSegment(sketch, "E745", {"start": v(-44.23, 24.31) * mm, "end": v(-43.14, 23.61) * mm});
            skLineSegment(sketch, "E746", {"start": v(-43.14, 23.61) * mm, "end": v(-42.9, 22.82) * mm});
            skLineSegment(sketch, "E747", {"start": v(-42.9, 22.82) * mm, "end": v(-41.58, 20.6) * mm});
            skLineSegment(sketch, "E748", {"start": v(-41.58, 20.6) * mm, "end": v(-40.81, 18.08) * mm});
            skLineSegment(sketch, "E749", {"start": v(-40.81, 18.08) * mm, "end": v(-40.31, 16.46) * mm});
            skLineSegment(sketch, "E750", {"start": v(-40.31, 16.46) * mm, "end": v(-39.79, 14.74) * mm});
            skLineSegment(sketch, "E751", {"start": v(-39.79, 14.74) * mm, "end": v(-38.6, 14.74) * mm});
            skLineSegment(sketch, "E752", {"start": v(-38.6, 14.74) * mm, "end": v(-36.9, 15.49) * mm});
            skLineSegment(sketch, "E753", {"start": v(-36.9, 15.49) * mm, "end": v(-36.03, 16) * mm});
            skLineSegment(sketch, "E754", {"start": v(-36.03, 16) * mm, "end": v(-35.61, 16.45) * mm});
            skSolve(sketch);
        }
        {
            var Q0;
            Q0=makeQuery(id+"F16.imprint","IMPRINT",FACE,{"disambiguationData":[TD([[makeQuery(id+"F16.imprint","IMPRINT",EDGE,{"derivedFrom":sQuery(id+"F16.wireOp",EDGE,"E629")}),1.0]])]});
            extrude(context, id + "F17", {"entities" : qUnion([Q0]), "depth" : 2.5 * mm, "offsetDistance" : 25 * mm});
        }
        {
            var Q0;
            Q0=qCreatedBy(makeId("Front.planeOp"),FACE);
            var sketch = newSketch(context, id + "F18", { "sketchPlane" : qUnion([Q0])});
            skText(sketch, "E755", { "text": "Strictly", "fontName": "Tinos-Regular.ttf"});
            const initialGuessF18  = {"E755": [-0.03386, 0.00227, 1, 0, 0.01462]};
            skSetInitialGuess(sketch, initialGuessF18);
            skSolve(sketch);
        }
        {
            var Q0;
            Q0 = qSketchRegion(id + "F18", true);
            extrude(context, id + "F19", {"entities" : qUnion([Q0]), "depth" : 3.5 * mm, "offsetDistance" : 25 * mm});
        }
        {
            var Q0;
            Q0=makeQuery(id+"F19.opExtrude","SWEPT_BODY",BODY,{"disambiguationData":[OSD([sQuery(id+"F18.wireOp",EDGE,"E755.sketch_text.stroke-74"),sQuery(id+"F18.wireOp",EDGE,"E755.sketch_text.stroke-75"),sQuery(id+"F18.wireOp",EDGE,"E755.sketch_text.stroke-76"),sQuery(id+"F18.wireOp",EDGE,"E755.sketch_text.stroke-77"),sQuery(id+"F18.wireOp",EDGE,"E755.sketch_text.stroke-78"),sQuery(id+"F18.wireOp",EDGE,"E755.sketch_text.stroke-79"),sQuery(id+"F18.wireOp",EDGE,"E755.sketch_text.stroke-80"),sQuery(id+"F18.wireOp",EDGE,"E755.sketch_text.stroke-81")])]});
            transform(context, id + "F20", {"entities" : qUnion([Q0]), "transformType" : TransformType.TRANSLATION_3D, "dx" : 0 * mm, "dy" : 0 * mm, "dz" : -2.04 * mm, "makeCopy" : false});
        }
        {
            var Q0;
            Q0=makeQuery(id+"F19.opExtrude","SWEPT_BODY",BODY,{"disambiguationData":[OSD([sQuery(id+"F18.wireOp",EDGE,"E755.sketch_text.stroke-136"),sQuery(id+"F18.wireOp",EDGE,"E755.sketch_text.stroke-137"),sQuery(id+"F18.wireOp",EDGE,"E755.sketch_text.stroke-138"),sQuery(id+"F18.wireOp",EDGE,"E755.sketch_text.stroke-139"),sQuery(id+"F18.wireOp",EDGE,"E755.sketch_text.stroke-140"),sQuery(id+"F18.wireOp",EDGE,"E755.sketch_text.stroke-141"),sQuery(id+"F18.wireOp",EDGE,"E755.sketch_text.stroke-142"),sQuery(id+"F18.wireOp",EDGE,"E755.sketch_text.stroke-143"),sQuery(id+"F18.wireOp",EDGE,"E755.sketch_text.stroke-144"),sQuery(id+"F18.wireOp",EDGE,"E755.sketch_text.stroke-145"),sQuery(id+"F18.wireOp",EDGE,"E755.sketch_text.stroke-146"),sQuery(id+"F18.wireOp",EDGE,"E755.sketch_text.stroke-147"),sQuery(id+"F18.wireOp",EDGE,"E755.sketch_text.stroke-148"),sQuery(id+"F18.wireOp",EDGE,"E755.sketch_text.stroke-149"),sQuery(id+"F18.wireOp",EDGE,"E755.sketch_text.stroke-150"),sQuery(id+"F18.wireOp",EDGE,"E755.sketch_text.stroke-151"),sQuery(id+"F18.wireOp",EDGE,"E755.sketch_text.stroke-152"),sQuery(id+"F18.wireOp",EDGE,"E755.sketch_text.stroke-153"),sQuery(id+"F18.wireOp",EDGE,"E755.sketch_text.stroke-154"),sQuery(id+"F18.wireOp",EDGE,"E755.sketch_text.stroke-155"),sQuery(id+"F18.wireOp",EDGE,"E755.sketch_text.stroke-156"),sQuery(id+"F18.wireOp",EDGE,"E755.sketch_text.stroke-157"),sQuery(id+"F18.wireOp",EDGE,"E755.sketch_text.stroke-158"),sQuery(id+"F18.wireOp",EDGE,"E755.sketch_text.stroke-159"),sQuery(id+"F18.wireOp",EDGE,"E755.sketch_text.stroke-160")])]});
            transform(context, id + "F21", {"entities" : qUnion([Q0]), "transformType" : TransformType.TRANSLATION_3D, "dx" : 0 * mm, "dy" : 0 * mm, "dz" : 4.3 * mm, "makeCopy" : false});
        }
        {
            var Q0;
            Q0=makeQuery(id+"F19.opExtrude","SWEPT_BODY",BODY,{"disambiguationData":[OSD([sQuery(id+"F18.wireOp",EDGE,"E755.sketch_text.stroke-136"),sQuery(id+"F18.wireOp",EDGE,"E755.sketch_text.stroke-137"),sQuery(id+"F18.wireOp",EDGE,"E755.sketch_text.stroke-138"),sQuery(id+"F18.wireOp",EDGE,"E755.sketch_text.stroke-139"),sQuery(id+"F18.wireOp",EDGE,"E755.sketch_text.stroke-140"),sQuery(id+"F18.wireOp",EDGE,"E755.sketch_text.stroke-141"),sQuery(id+"F18.wireOp",EDGE,"E755.sketch_text.stroke-142"),sQuery(id+"F18.wireOp",EDGE,"E755.sketch_text.stroke-143"),sQuery(id+"F18.wireOp",EDGE,"E755.sketch_text.stroke-144"),sQuery(id+"F18.wireOp",EDGE,"E755.sketch_text.stroke-145"),sQuery(id+"F18.wireOp",EDGE,"E755.sketch_text.stroke-146"),sQuery(id+"F18.wireOp",EDGE,"E755.sketch_text.stroke-147"),sQuery(id+"F18.wireOp",EDGE,"E755.sketch_text.stroke-148"),sQuery(id+"F18.wireOp",EDGE,"E755.sketch_text.stroke-149"),sQuery(id+"F18.wireOp",EDGE,"E755.sketch_text.stroke-150"),sQuery(id+"F18.wireOp",EDGE,"E755.sketch_text.stroke-151"),sQuery(id+"F18.wireOp",EDGE,"E755.sketch_text.stroke-152"),sQuery(id+"F18.wireOp",EDGE,"E755.sketch_text.stroke-153"),sQuery(id+"F18.wireOp",EDGE,"E755.sketch_text.stroke-154"),sQuery(id+"F18.wireOp",EDGE,"E755.sketch_text.stroke-155"),sQuery(id+"F18.wireOp",EDGE,"E755.sketch_text.stroke-156"),sQuery(id+"F18.wireOp",EDGE,"E755.sketch_text.stroke-157"),sQuery(id+"F18.wireOp",EDGE,"E755.sketch_text.stroke-158"),sQuery(id+"F18.wireOp",EDGE,"E755.sketch_text.stroke-159"),sQuery(id+"F18.wireOp",EDGE,"E755.sketch_text.stroke-160")])]});
            var Q1;
            Q1=makeQuery(id+"F19.opExtrude","CAP_VERTEX",VERTEX,{"disambiguationData":[OSD([sQuery(id+"F18.wireOp",EDGE,"E755.sketch_text.stroke-136"),sQuery(id+"F18.wireOp",EDGE,"E755.sketch_text.stroke-160")])],"isStart":false});
            transform(context, id + "F22", {"entities" : qUnion([Q0]), "transformType" : TransformType.SCALE_UNIFORMLY, "scale" : .80, "scalePoint" : qUnion([Q1]), "makeCopy" : false});
        }
        {
            var Q0;
            Q0=makeQuery(id+"F19.opExtrude","SWEPT_BODY",BODY,{"disambiguationData":[OSD([sQuery(id+"F18.wireOp",EDGE,"E755.sketch_text.stroke-0"),sQuery(id+"F18.wireOp",EDGE,"E755.sketch_text.stroke-1"),sQuery(id+"F18.wireOp",EDGE,"E755.sketch_text.stroke-2"),sQuery(id+"F18.wireOp",EDGE,"E755.sketch_text.stroke-3"),sQuery(id+"F18.wireOp",EDGE,"E755.sketch_text.stroke-4"),sQuery(id+"F18.wireOp",EDGE,"E755.sketch_text.stroke-5"),sQuery(id+"F18.wireOp",EDGE,"E755.sketch_text.stroke-6"),sQuery(id+"F18.wireOp",EDGE,"E755.sketch_text.stroke-7"),sQuery(id+"F18.wireOp",EDGE,"E755.sketch_text.stroke-8"),sQuery(id+"F18.wireOp",EDGE,"E755.sketch_text.stroke-9"),sQuery(id+"F18.wireOp",EDGE,"E755.sketch_text.stroke-10"),sQuery(id+"F18.wireOp",EDGE,"E755.sketch_text.stroke-11"),sQuery(id+"F18.wireOp",EDGE,"E755.sketch_text.stroke-12"),sQuery(id+"F18.wireOp",EDGE,"E755.sketch_text.stroke-13"),sQuery(id+"F18.wireOp",EDGE,"E755.sketch_text.stroke-14"),sQuery(id+"F18.wireOp",EDGE,"E755.sketch_text.stroke-15"),sQuery(id+"F18.wireOp",EDGE,"E755.sketch_text.stroke-16"),sQuery(id+"F18.wireOp",EDGE,"E755.sketch_text.stroke-17"),sQuery(id+"F18.wireOp",EDGE,"E755.sketch_text.stroke-18"),sQuery(id+"F18.wireOp",EDGE,"E755.sketch_text.stroke-19"),sQuery(id+"F18.wireOp",EDGE,"E755.sketch_text.stroke-20"),sQuery(id+"F18.wireOp",EDGE,"E755.sketch_text.stroke-21"),sQuery(id+"F18.wireOp",EDGE,"E755.sketch_text.stroke-22"),sQuery(id+"F18.wireOp",EDGE,"E755.sketch_text.stroke-23"),sQuery(id+"F18.wireOp",EDGE,"E755.sketch_text.stroke-24"),sQuery(id+"F18.wireOp",EDGE,"E755.sketch_text.stroke-25"),sQuery(id+"F18.wireOp",EDGE,"E755.sketch_text.stroke-26"),sQuery(id+"F18.wireOp",EDGE,"E755.sketch_text.stroke-27"),sQuery(id+"F18.wireOp",EDGE,"E755.sketch_text.stroke-28"),sQuery(id+"F18.wireOp",EDGE,"E755.sketch_text.stroke-29"),sQuery(id+"F18.wireOp",EDGE,"E755.sketch_text.stroke-30"),sQuery(id+"F18.wireOp",EDGE,"E755.sketch_text.stroke-31"),sQuery(id+"F18.wireOp",EDGE,"E755.sketch_text.stroke-32"),sQuery(id+"F18.wireOp",EDGE,"E755.sketch_text.stroke-33"),sQuery(id+"F18.wireOp",EDGE,"E755.sketch_text.stroke-34"),sQuery(id+"F18.wireOp",EDGE,"E755.sketch_text.stroke-35")])]});
            var Q1;
            Q1=makeQuery(id+"F19.opExtrude","SWEPT_BODY",BODY,{"disambiguationData":[OSD([sQuery(id+"F18.wireOp",EDGE,"E755.sketch_text.stroke-36"),sQuery(id+"F18.wireOp",EDGE,"E755.sketch_text.stroke-37"),sQuery(id+"F18.wireOp",EDGE,"E755.sketch_text.stroke-38"),sQuery(id+"F18.wireOp",EDGE,"E755.sketch_text.stroke-39"),sQuery(id+"F18.wireOp",EDGE,"E755.sketch_text.stroke-40"),sQuery(id+"F18.wireOp",EDGE,"E755.sketch_text.stroke-41"),sQuery(id+"F18.wireOp",EDGE,"E755.sketch_text.stroke-42"),sQuery(id+"F18.wireOp",EDGE,"E755.sketch_text.stroke-43"),sQuery(id+"F18.wireOp",EDGE,"E755.sketch_text.stroke-44"),sQuery(id+"F18.wireOp",EDGE,"E755.sketch_text.stroke-45"),sQuery(id+"F18.wireOp",EDGE,"E755.sketch_text.stroke-46"),sQuery(id+"F18.wireOp",EDGE,"E755.sketch_text.stroke-47"),sQuery(id+"F18.wireOp",EDGE,"E755.sketch_text.stroke-48"),sQuery(id+"F18.wireOp",EDGE,"E755.sketch_text.stroke-49"),sQuery(id+"F18.wireOp",EDGE,"E755.sketch_text.stroke-50"),sQuery(id+"F18.wireOp",EDGE,"E755.sketch_text.stroke-51"),sQuery(id+"F18.wireOp",EDGE,"E755.sketch_text.stroke-52"),sQuery(id+"F18.wireOp",EDGE,"E755.sketch_text.stroke-53"),sQuery(id+"F18.wireOp",EDGE,"E755.sketch_text.stroke-54")])]});
            var Q2;
            Q2=makeQuery(id+"F19.opExtrude","SWEPT_BODY",BODY,{"disambiguationData":[OSD([sQuery(id+"F18.wireOp",EDGE,"E755.sketch_text.stroke-55"),sQuery(id+"F18.wireOp",EDGE,"E755.sketch_text.stroke-56"),sQuery(id+"F18.wireOp",EDGE,"E755.sketch_text.stroke-57"),sQuery(id+"F18.wireOp",EDGE,"E755.sketch_text.stroke-58"),sQuery(id+"F18.wireOp",EDGE,"E755.sketch_text.stroke-59"),sQuery(id+"F18.wireOp",EDGE,"E755.sketch_text.stroke-60"),sQuery(id+"F18.wireOp",EDGE,"E755.sketch_text.stroke-61"),sQuery(id+"F18.wireOp",EDGE,"E755.sketch_text.stroke-62"),sQuery(id+"F18.wireOp",EDGE,"E755.sketch_text.stroke-63"),sQuery(id+"F18.wireOp",EDGE,"E755.sketch_text.stroke-64"),sQuery(id+"F18.wireOp",EDGE,"E755.sketch_text.stroke-65"),sQuery(id+"F18.wireOp",EDGE,"E755.sketch_text.stroke-66"),sQuery(id+"F18.wireOp",EDGE,"E755.sketch_text.stroke-67"),sQuery(id+"F18.wireOp",EDGE,"E755.sketch_text.stroke-68"),sQuery(id+"F18.wireOp",EDGE,"E755.sketch_text.stroke-69"),sQuery(id+"F18.wireOp",EDGE,"E755.sketch_text.stroke-70"),sQuery(id+"F18.wireOp",EDGE,"E755.sketch_text.stroke-71"),sQuery(id+"F18.wireOp",EDGE,"E755.sketch_text.stroke-72"),sQuery(id+"F18.wireOp",EDGE,"E755.sketch_text.stroke-73")])]});
            var Q3;
            Q3=makeQuery(id+"F19.opExtrude","SWEPT_BODY",BODY,{"disambiguationData":[OSD([sQuery(id+"F18.wireOp",EDGE,"E755.sketch_text.stroke-82"),sQuery(id+"F18.wireOp",EDGE,"E755.sketch_text.stroke-83"),sQuery(id+"F18.wireOp",EDGE,"E755.sketch_text.stroke-84"),sQuery(id+"F18.wireOp",EDGE,"E755.sketch_text.stroke-85"),sQuery(id+"F18.wireOp",EDGE,"E755.sketch_text.stroke-86"),sQuery(id+"F18.wireOp",EDGE,"E755.sketch_text.stroke-87"),sQuery(id+"F18.wireOp",EDGE,"E755.sketch_text.stroke-88"),sQuery(id+"F18.wireOp",EDGE,"E755.sketch_text.stroke-89"),sQuery(id+"F18.wireOp",EDGE,"E755.sketch_text.stroke-90"),sQuery(id+"F18.wireOp",EDGE,"E755.sketch_text.stroke-91")])]});
            var Q4;
            Q4=makeQuery(id+"F19.opExtrude","SWEPT_BODY",BODY,{"disambiguationData":[OSD([sQuery(id+"F18.wireOp",EDGE,"E755.sketch_text.stroke-74"),sQuery(id+"F18.wireOp",EDGE,"E755.sketch_text.stroke-75"),sQuery(id+"F18.wireOp",EDGE,"E755.sketch_text.stroke-76"),sQuery(id+"F18.wireOp",EDGE,"E755.sketch_text.stroke-77"),sQuery(id+"F18.wireOp",EDGE,"E755.sketch_text.stroke-78"),sQuery(id+"F18.wireOp",EDGE,"E755.sketch_text.stroke-79"),sQuery(id+"F18.wireOp",EDGE,"E755.sketch_text.stroke-80"),sQuery(id+"F18.wireOp",EDGE,"E755.sketch_text.stroke-81")])]});
            var Q5;
            Q5=makeQuery(id+"F19.opExtrude","SWEPT_BODY",BODY,{"disambiguationData":[OSD([sQuery(id+"F18.wireOp",EDGE,"E755.sketch_text.stroke-92"),sQuery(id+"F18.wireOp",EDGE,"E755.sketch_text.stroke-93"),sQuery(id+"F18.wireOp",EDGE,"E755.sketch_text.stroke-94"),sQuery(id+"F18.wireOp",EDGE,"E755.sketch_text.stroke-95"),sQuery(id+"F18.wireOp",EDGE,"E755.sketch_text.stroke-96"),sQuery(id+"F18.wireOp",EDGE,"E755.sketch_text.stroke-97"),sQuery(id+"F18.wireOp",EDGE,"E755.sketch_text.stroke-98"),sQuery(id+"F18.wireOp",EDGE,"E755.sketch_text.stroke-99"),sQuery(id+"F18.wireOp",EDGE,"E755.sketch_text.stroke-100"),sQuery(id+"F18.wireOp",EDGE,"E755.sketch_text.stroke-101"),sQuery(id+"F18.wireOp",EDGE,"E755.sketch_text.stroke-102"),sQuery(id+"F18.wireOp",EDGE,"E755.sketch_text.stroke-103"),sQuery(id+"F18.wireOp",EDGE,"E755.sketch_text.stroke-104"),sQuery(id+"F18.wireOp",EDGE,"E755.sketch_text.stroke-105"),sQuery(id+"F18.wireOp",EDGE,"E755.sketch_text.stroke-106")])]});
            var Q6;
            Q6=makeQuery(id+"F19.opExtrude","SWEPT_BODY",BODY,{"disambiguationData":[OSD([sQuery(id+"F18.wireOp",EDGE,"E755.sketch_text.stroke-107"),sQuery(id+"F18.wireOp",EDGE,"E755.sketch_text.stroke-108"),sQuery(id+"F18.wireOp",EDGE,"E755.sketch_text.stroke-109"),sQuery(id+"F18.wireOp",EDGE,"E755.sketch_text.stroke-110"),sQuery(id+"F18.wireOp",EDGE,"E755.sketch_text.stroke-111"),sQuery(id+"F18.wireOp",EDGE,"E755.sketch_text.stroke-112"),sQuery(id+"F18.wireOp",EDGE,"E755.sketch_text.stroke-113"),sQuery(id+"F18.wireOp",EDGE,"E755.sketch_text.stroke-114"),sQuery(id+"F18.wireOp",EDGE,"E755.sketch_text.stroke-115"),sQuery(id+"F18.wireOp",EDGE,"E755.sketch_text.stroke-116"),sQuery(id+"F18.wireOp",EDGE,"E755.sketch_text.stroke-117"),sQuery(id+"F18.wireOp",EDGE,"E755.sketch_text.stroke-118"),sQuery(id+"F18.wireOp",EDGE,"E755.sketch_text.stroke-119"),sQuery(id+"F18.wireOp",EDGE,"E755.sketch_text.stroke-120"),sQuery(id+"F18.wireOp",EDGE,"E755.sketch_text.stroke-121"),sQuery(id+"F18.wireOp",EDGE,"E755.sketch_text.stroke-122"),sQuery(id+"F18.wireOp",EDGE,"E755.sketch_text.stroke-123"),sQuery(id+"F18.wireOp",EDGE,"E755.sketch_text.stroke-124"),sQuery(id+"F18.wireOp",EDGE,"E755.sketch_text.stroke-125")])]});
            var Q7;
            Q7=makeQuery(id+"F19.opExtrude","SWEPT_BODY",BODY,{"disambiguationData":[OSD([sQuery(id+"F18.wireOp",EDGE,"E755.sketch_text.stroke-126"),sQuery(id+"F18.wireOp",EDGE,"E755.sketch_text.stroke-127"),sQuery(id+"F18.wireOp",EDGE,"E755.sketch_text.stroke-128"),sQuery(id+"F18.wireOp",EDGE,"E755.sketch_text.stroke-129"),sQuery(id+"F18.wireOp",EDGE,"E755.sketch_text.stroke-130"),sQuery(id+"F18.wireOp",EDGE,"E755.sketch_text.stroke-131"),sQuery(id+"F18.wireOp",EDGE,"E755.sketch_text.stroke-132"),sQuery(id+"F18.wireOp",EDGE,"E755.sketch_text.stroke-133"),sQuery(id+"F18.wireOp",EDGE,"E755.sketch_text.stroke-134"),sQuery(id+"F18.wireOp",EDGE,"E755.sketch_text.stroke-135")])]});
            var Q8;
            Q8=makeQuery(id+"F19.opExtrude","SWEPT_BODY",BODY,{"disambiguationData":[OSD([sQuery(id+"F18.wireOp",EDGE,"E755.sketch_text.stroke-136"),sQuery(id+"F18.wireOp",EDGE,"E755.sketch_text.stroke-137"),sQuery(id+"F18.wireOp",EDGE,"E755.sketch_text.stroke-138"),sQuery(id+"F18.wireOp",EDGE,"E755.sketch_text.stroke-139"),sQuery(id+"F18.wireOp",EDGE,"E755.sketch_text.stroke-140"),sQuery(id+"F18.wireOp",EDGE,"E755.sketch_text.stroke-141"),sQuery(id+"F18.wireOp",EDGE,"E755.sketch_text.stroke-142"),sQuery(id+"F18.wireOp",EDGE,"E755.sketch_text.stroke-143"),sQuery(id+"F18.wireOp",EDGE,"E755.sketch_text.stroke-144"),sQuery(id+"F18.wireOp",EDGE,"E755.sketch_text.stroke-145"),sQuery(id+"F18.wireOp",EDGE,"E755.sketch_text.stroke-146"),sQuery(id+"F18.wireOp",EDGE,"E755.sketch_text.stroke-147"),sQuery(id+"F18.wireOp",EDGE,"E755.sketch_text.stroke-148"),sQuery(id+"F18.wireOp",EDGE,"E755.sketch_text.stroke-149"),sQuery(id+"F18.wireOp",EDGE,"E755.sketch_text.stroke-150"),sQuery(id+"F18.wireOp",EDGE,"E755.sketch_text.stroke-151"),sQuery(id+"F18.wireOp",EDGE,"E755.sketch_text.stroke-152"),sQuery(id+"F18.wireOp",EDGE,"E755.sketch_text.stroke-153"),sQuery(id+"F18.wireOp",EDGE,"E755.sketch_text.stroke-154"),sQuery(id+"F18.wireOp",EDGE,"E755.sketch_text.stroke-155"),sQuery(id+"F18.wireOp",EDGE,"E755.sketch_text.stroke-156"),sQuery(id+"F18.wireOp",EDGE,"E755.sketch_text.stroke-157"),sQuery(id+"F18.wireOp",EDGE,"E755.sketch_text.stroke-158"),sQuery(id+"F18.wireOp",EDGE,"E755.sketch_text.stroke-159"),sQuery(id+"F18.wireOp",EDGE,"E755.sketch_text.stroke-160")])]});
            transform(context, id + "F23", {"entities" : qUnion([Q0, Q1, Q2, Q3, Q4, Q5, Q6, Q7, Q8]), "transformType" : TransformType.TRANSLATION_3D, "dx" : -2 * mm, "dy" : 0 * mm, "dz" : -0.8 * mm, "makeCopy" : false});
        }
        {
            var Q0;
            Q0=qCreatedBy(makeId("Front.planeOp"),FACE);
            var sketch = newSketch(context, id + "F24", { "sketchPlane" : qUnion([Q0])});
            skLineSegment(sketch, "E756.bottom", {"start": v(-70.75, 1.7) * mm, "end": v(68.75, 1.7) * mm});
            skLineSegment(sketch, "E756.top", {"start": v(-70.75, -2.2) * mm, "end": v(68.75, -2.2) * mm});
            skLineSegment(sketch, "E756.left", {"start": v(-70.75, 1.7) * mm, "end": v(-70.75, -2.2) * mm});
            skLineSegment(sketch, "E756.right", {"start": v(68.75, 1.7) * mm, "end": v(68.75, -2.2) * mm});
            skSolve(sketch);
        }
        {
            var Q0;
            Q0=makeQuery(id+"F24.imprint","IMPRINT",FACE,{"disambiguationData":[TD([[makeQuery(id+"F24.imprint","IMPRINT",EDGE,{"derivedFrom":sQuery(id+"F24.wireOp",EDGE,"E756.bottom")}),-1.0]])]});
            extrude(context, id + "F25", {"entities" : qUnion([Q0]), "depth" : 9.2 * mm, "offsetDistance" : 25 * mm});
        }
        {
            var Q0;
            Q0=makeQuery(id+"F25.opExtrude","CAP_EDGE",EDGE,{"disambiguationData":[OSD([sQuery(id+"F24.wireOp",EDGE,"E756.top")])],"isStart":false});
            chamfer(context, id + "F26", {"entities" : qUnion([Q0]), "width" : 4.5 * mm, "tangentPropagation" : true});
        }
        {
            var Q0;
            Q0=makeQuery(id+"F15.opExtrude","SWEPT_BODY",BODY,{"disambiguationData":[OSD([sQuery(id+"F14.wireOp",EDGE,"E522"),sQuery(id+"F14.wireOp",EDGE,"E523"),sQuery(id+"F14.wireOp",EDGE,"E524"),sQuery(id+"F14.wireOp",EDGE,"E525"),sQuery(id+"F14.wireOp",EDGE,"E526"),sQuery(id+"F14.wireOp",EDGE,"E527"),sQuery(id+"F14.wireOp",EDGE,"E528"),sQuery(id+"F14.wireOp",EDGE,"E529"),sQuery(id+"F14.wireOp",EDGE,"E530"),sQuery(id+"F14.wireOp",EDGE,"E531"),sQuery(id+"F14.wireOp",EDGE,"E532"),sQuery(id+"F14.wireOp",EDGE,"E533"),sQuery(id+"F14.wireOp",EDGE,"E534"),sQuery(id+"F14.wireOp",EDGE,"E535"),sQuery(id+"F14.wireOp",EDGE,"E536"),sQuery(id+"F14.wireOp",EDGE,"E537"),sQuery(id+"F14.wireOp",EDGE,"E538"),sQuery(id+"F14.wireOp",EDGE,"E539"),sQuery(id+"F14.wireOp",EDGE,"E540"),sQuery(id+"F14.wireOp",EDGE,"E541"),sQuery(id+"F14.wireOp",EDGE,"E542"),sQuery(id+"F14.wireOp",EDGE,"E543"),sQuery(id+"F14.wireOp",EDGE,"E544"),sQuery(id+"F14.wireOp",EDGE,"E545"),sQuery(id+"F14.wireOp",EDGE,"E546"),sQuery(id+"F14.wireOp",EDGE,"E547"),sQuery(id+"F14.wireOp",EDGE,"E548"),sQuery(id+"F14.wireOp",EDGE,"E549"),sQuery(id+"F14.wireOp",EDGE,"E550"),sQuery(id+"F14.wireOp",EDGE,"E551"),sQuery(id+"F14.wireOp",EDGE,"E552"),sQuery(id+"F14.wireOp",EDGE,"E553"),sQuery(id+"F14.wireOp",EDGE,"E554"),sQuery(id+"F14.wireOp",EDGE,"E555"),sQuery(id+"F14.wireOp",EDGE,"E556"),sQuery(id+"F14.wireOp",EDGE,"E557"),sQuery(id+"F14.wireOp",EDGE,"E558"),sQuery(id+"F14.wireOp",EDGE,"E559"),sQuery(id+"F14.wireOp",EDGE,"E560"),sQuery(id+"F14.wireOp",EDGE,"E561"),sQuery(id+"F14.wireOp",EDGE,"E562"),sQuery(id+"F14.wireOp",EDGE,"E563"),sQuery(id+"F14.wireOp",EDGE,"E564"),sQuery(id+"F14.wireOp",EDGE,"E565"),sQuery(id+"F14.wireOp",EDGE,"E566"),sQuery(id+"F14.wireOp",EDGE,"E567"),sQuery(id+"F14.wireOp",EDGE,"E568"),sQuery(id+"F14.wireOp",EDGE,"E569"),sQuery(id+"F14.wireOp",EDGE,"E570"),sQuery(id+"F14.wireOp",EDGE,"E571"),sQuery(id+"F14.wireOp",EDGE,"E572"),sQuery(id+"F14.wireOp",EDGE,"E573"),sQuery(id+"F14.wireOp",EDGE,"E574"),sQuery(id+"F14.wireOp",EDGE,"E575"),sQuery(id+"F14.wireOp",EDGE,"E576"),sQuery(id+"F14.wireOp",EDGE,"E577"),sQuery(id+"F14.wireOp",EDGE,"E578"),sQuery(id+"F14.wireOp",EDGE,"E579"),sQuery(id+"F14.wireOp",EDGE,"E580"),sQuery(id+"F14.wireOp",EDGE,"E581"),sQuery(id+"F14.wireOp",EDGE,"E582"),sQuery(id+"F14.wireOp",EDGE,"E583"),sQuery(id+"F14.wireOp",EDGE,"E584"),sQuery(id+"F14.wireOp",EDGE,"E585"),sQuery(id+"F14.wireOp",EDGE,"E586"),sQuery(id+"F14.wireOp",EDGE,"E587"),sQuery(id+"F14.wireOp",EDGE,"E588"),sQuery(id+"F14.wireOp",EDGE,"E589"),sQuery(id+"F14.wireOp",EDGE,"E590"),sQuery(id+"F14.wireOp",EDGE,"E591"),sQuery(id+"F14.wireOp",EDGE,"E592"),sQuery(id+"F14.wireOp",EDGE,"E593"),sQuery(id+"F14.wireOp",EDGE,"E594"),sQuery(id+"F14.wireOp",EDGE,"E595"),sQuery(id+"F14.wireOp",EDGE,"E596"),sQuery(id+"F14.wireOp",EDGE,"E597"),sQuery(id+"F14.wireOp",EDGE,"E598"),sQuery(id+"F14.wireOp",EDGE,"E599"),sQuery(id+"F14.wireOp",EDGE,"E600"),sQuery(id+"F14.wireOp",EDGE,"E601"),sQuery(id+"F14.wireOp",EDGE,"E602"),sQuery(id+"F14.wireOp",EDGE,"E603"),sQuery(id+"F14.wireOp",EDGE,"E604"),sQuery(id+"F14.wireOp",EDGE,"E605"),sQuery(id+"F14.wireOp",EDGE,"E606"),sQuery(id+"F14.wireOp",EDGE,"E607"),sQuery(id+"F14.wireOp",EDGE,"E608"),sQuery(id+"F14.wireOp",EDGE,"E609"),sQuery(id+"F14.wireOp",EDGE,"E610"),sQuery(id+"F14.wireOp",EDGE,"E611"),sQuery(id+"F14.wireOp",EDGE,"E612"),sQuery(id+"F14.wireOp",EDGE,"E613"),sQuery(id+"F14.wireOp",EDGE,"E614"),sQuery(id+"F14.wireOp",EDGE,"E615"),sQuery(id+"F14.wireOp",EDGE,"E616"),sQuery(id+"F14.wireOp",EDGE,"E617"),sQuery(id+"F14.wireOp",EDGE,"E618"),sQuery(id+"F14.wireOp",EDGE,"E619"),sQuery(id+"F14.wireOp",EDGE,"E620"),sQuery(id+"F14.wireOp",EDGE,"E621"),sQuery(id+"F14.wireOp",EDGE,"E622"),sQuery(id+"F14.wireOp",EDGE,"E623"),sQuery(id+"F14.wireOp",EDGE,"E624"),sQuery(id+"F14.wireOp",EDGE,"E625"),sQuery(id+"F14.wireOp",EDGE,"E626"),sQuery(id+"F14.wireOp",EDGE,"E627"),sQuery(id+"F14.wireOp",EDGE,"E628")])]});
            var Q1;
            Q1=makeQuery(id+"F15.opExtrude","CAP_VERTEX",VERTEX,{"disambiguationData":[OSD([sQuery(id+"F14.wireOp",EDGE,"E576"),sQuery(id+"F14.wireOp",EDGE,"E577")])],"isStart":true});
            transform(context, id + "F27", {"entities" : qUnion([Q0]), "transformType" : TransformType.SCALE_UNIFORMLY, "scale" : 1.3, "scalePoint" : qUnion([Q1]), "makeCopy" : false});
        }
        {
            var Q0;
            Q0=makeQuery(id+"F19.opExtrude","SWEPT_BODY",BODY,{"disambiguationData":[OSD([sQuery(id+"F18.wireOp",EDGE,"E755.sketch_text.stroke-0"),sQuery(id+"F18.wireOp",EDGE,"E755.sketch_text.stroke-1"),sQuery(id+"F18.wireOp",EDGE,"E755.sketch_text.stroke-2"),sQuery(id+"F18.wireOp",EDGE,"E755.sketch_text.stroke-3"),sQuery(id+"F18.wireOp",EDGE,"E755.sketch_text.stroke-4"),sQuery(id+"F18.wireOp",EDGE,"E755.sketch_text.stroke-5"),sQuery(id+"F18.wireOp",EDGE,"E755.sketch_text.stroke-6"),sQuery(id+"F18.wireOp",EDGE,"E755.sketch_text.stroke-7"),sQuery(id+"F18.wireOp",EDGE,"E755.sketch_text.stroke-8"),sQuery(id+"F18.wireOp",EDGE,"E755.sketch_text.stroke-9"),sQuery(id+"F18.wireOp",EDGE,"E755.sketch_text.stroke-10"),sQuery(id+"F18.wireOp",EDGE,"E755.sketch_text.stroke-11"),sQuery(id+"F18.wireOp",EDGE,"E755.sketch_text.stroke-12"),sQuery(id+"F18.wireOp",EDGE,"E755.sketch_text.stroke-13"),sQuery(id+"F18.wireOp",EDGE,"E755.sketch_text.stroke-14"),sQuery(id+"F18.wireOp",EDGE,"E755.sketch_text.stroke-15"),sQuery(id+"F18.wireOp",EDGE,"E755.sketch_text.stroke-16"),sQuery(id+"F18.wireOp",EDGE,"E755.sketch_text.stroke-17"),sQuery(id+"F18.wireOp",EDGE,"E755.sketch_text.stroke-18"),sQuery(id+"F18.wireOp",EDGE,"E755.sketch_text.stroke-19"),sQuery(id+"F18.wireOp",EDGE,"E755.sketch_text.stroke-20"),sQuery(id+"F18.wireOp",EDGE,"E755.sketch_text.stroke-21"),sQuery(id+"F18.wireOp",EDGE,"E755.sketch_text.stroke-22"),sQuery(id+"F18.wireOp",EDGE,"E755.sketch_text.stroke-23"),sQuery(id+"F18.wireOp",EDGE,"E755.sketch_text.stroke-24"),sQuery(id+"F18.wireOp",EDGE,"E755.sketch_text.stroke-25"),sQuery(id+"F18.wireOp",EDGE,"E755.sketch_text.stroke-26"),sQuery(id+"F18.wireOp",EDGE,"E755.sketch_text.stroke-27"),sQuery(id+"F18.wireOp",EDGE,"E755.sketch_text.stroke-28"),sQuery(id+"F18.wireOp",EDGE,"E755.sketch_text.stroke-29"),sQuery(id+"F18.wireOp",EDGE,"E755.sketch_text.stroke-30"),sQuery(id+"F18.wireOp",EDGE,"E755.sketch_text.stroke-31"),sQuery(id+"F18.wireOp",EDGE,"E755.sketch_text.stroke-32"),sQuery(id+"F18.wireOp",EDGE,"E755.sketch_text.stroke-33"),sQuery(id+"F18.wireOp",EDGE,"E755.sketch_text.stroke-34"),sQuery(id+"F18.wireOp",EDGE,"E755.sketch_text.stroke-35")])]});
            var Q1;
            Q1=makeQuery(id+"F19.opExtrude","SWEPT_BODY",BODY,{"disambiguationData":[OSD([sQuery(id+"F18.wireOp",EDGE,"E755.sketch_text.stroke-36"),sQuery(id+"F18.wireOp",EDGE,"E755.sketch_text.stroke-37"),sQuery(id+"F18.wireOp",EDGE,"E755.sketch_text.stroke-38"),sQuery(id+"F18.wireOp",EDGE,"E755.sketch_text.stroke-39"),sQuery(id+"F18.wireOp",EDGE,"E755.sketch_text.stroke-40"),sQuery(id+"F18.wireOp",EDGE,"E755.sketch_text.stroke-41"),sQuery(id+"F18.wireOp",EDGE,"E755.sketch_text.stroke-42"),sQuery(id+"F18.wireOp",EDGE,"E755.sketch_text.stroke-43"),sQuery(id+"F18.wireOp",EDGE,"E755.sketch_text.stroke-44"),sQuery(id+"F18.wireOp",EDGE,"E755.sketch_text.stroke-45"),sQuery(id+"F18.wireOp",EDGE,"E755.sketch_text.stroke-46"),sQuery(id+"F18.wireOp",EDGE,"E755.sketch_text.stroke-47"),sQuery(id+"F18.wireOp",EDGE,"E755.sketch_text.stroke-48"),sQuery(id+"F18.wireOp",EDGE,"E755.sketch_text.stroke-49"),sQuery(id+"F18.wireOp",EDGE,"E755.sketch_text.stroke-50"),sQuery(id+"F18.wireOp",EDGE,"E755.sketch_text.stroke-51"),sQuery(id+"F18.wireOp",EDGE,"E755.sketch_text.stroke-52"),sQuery(id+"F18.wireOp",EDGE,"E755.sketch_text.stroke-53"),sQuery(id+"F18.wireOp",EDGE,"E755.sketch_text.stroke-54")])]});
            var Q2;
            Q2=makeQuery(id+"F19.opExtrude","SWEPT_BODY",BODY,{"disambiguationData":[OSD([sQuery(id+"F18.wireOp",EDGE,"E755.sketch_text.stroke-55"),sQuery(id+"F18.wireOp",EDGE,"E755.sketch_text.stroke-56"),sQuery(id+"F18.wireOp",EDGE,"E755.sketch_text.stroke-57"),sQuery(id+"F18.wireOp",EDGE,"E755.sketch_text.stroke-58"),sQuery(id+"F18.wireOp",EDGE,"E755.sketch_text.stroke-59"),sQuery(id+"F18.wireOp",EDGE,"E755.sketch_text.stroke-60"),sQuery(id+"F18.wireOp",EDGE,"E755.sketch_text.stroke-61"),sQuery(id+"F18.wireOp",EDGE,"E755.sketch_text.stroke-62"),sQuery(id+"F18.wireOp",EDGE,"E755.sketch_text.stroke-63"),sQuery(id+"F18.wireOp",EDGE,"E755.sketch_text.stroke-64"),sQuery(id+"F18.wireOp",EDGE,"E755.sketch_text.stroke-65"),sQuery(id+"F18.wireOp",EDGE,"E755.sketch_text.stroke-66"),sQuery(id+"F18.wireOp",EDGE,"E755.sketch_text.stroke-67"),sQuery(id+"F18.wireOp",EDGE,"E755.sketch_text.stroke-68"),sQuery(id+"F18.wireOp",EDGE,"E755.sketch_text.stroke-69"),sQuery(id+"F18.wireOp",EDGE,"E755.sketch_text.stroke-70"),sQuery(id+"F18.wireOp",EDGE,"E755.sketch_text.stroke-71"),sQuery(id+"F18.wireOp",EDGE,"E755.sketch_text.stroke-72"),sQuery(id+"F18.wireOp",EDGE,"E755.sketch_text.stroke-73")])]});
            var Q3;
            Q3=makeQuery(id+"F19.opExtrude","SWEPT_BODY",BODY,{"disambiguationData":[OSD([sQuery(id+"F18.wireOp",EDGE,"E755.sketch_text.stroke-74"),sQuery(id+"F18.wireOp",EDGE,"E755.sketch_text.stroke-75"),sQuery(id+"F18.wireOp",EDGE,"E755.sketch_text.stroke-76"),sQuery(id+"F18.wireOp",EDGE,"E755.sketch_text.stroke-77"),sQuery(id+"F18.wireOp",EDGE,"E755.sketch_text.stroke-78"),sQuery(id+"F18.wireOp",EDGE,"E755.sketch_text.stroke-79"),sQuery(id+"F18.wireOp",EDGE,"E755.sketch_text.stroke-80"),sQuery(id+"F18.wireOp",EDGE,"E755.sketch_text.stroke-81")])]});
            var Q4;
            Q4=makeQuery(id+"F19.opExtrude","SWEPT_BODY",BODY,{"disambiguationData":[OSD([sQuery(id+"F18.wireOp",EDGE,"E755.sketch_text.stroke-82"),sQuery(id+"F18.wireOp",EDGE,"E755.sketch_text.stroke-83"),sQuery(id+"F18.wireOp",EDGE,"E755.sketch_text.stroke-84"),sQuery(id+"F18.wireOp",EDGE,"E755.sketch_text.stroke-85"),sQuery(id+"F18.wireOp",EDGE,"E755.sketch_text.stroke-86"),sQuery(id+"F18.wireOp",EDGE,"E755.sketch_text.stroke-87"),sQuery(id+"F18.wireOp",EDGE,"E755.sketch_text.stroke-88"),sQuery(id+"F18.wireOp",EDGE,"E755.sketch_text.stroke-89"),sQuery(id+"F18.wireOp",EDGE,"E755.sketch_text.stroke-90"),sQuery(id+"F18.wireOp",EDGE,"E755.sketch_text.stroke-91")])]});
            var Q5;
            Q5=makeQuery(id+"F19.opExtrude","SWEPT_BODY",BODY,{"disambiguationData":[OSD([sQuery(id+"F18.wireOp",EDGE,"E755.sketch_text.stroke-92"),sQuery(id+"F18.wireOp",EDGE,"E755.sketch_text.stroke-93"),sQuery(id+"F18.wireOp",EDGE,"E755.sketch_text.stroke-94"),sQuery(id+"F18.wireOp",EDGE,"E755.sketch_text.stroke-95"),sQuery(id+"F18.wireOp",EDGE,"E755.sketch_text.stroke-96"),sQuery(id+"F18.wireOp",EDGE,"E755.sketch_text.stroke-97"),sQuery(id+"F18.wireOp",EDGE,"E755.sketch_text.stroke-98"),sQuery(id+"F18.wireOp",EDGE,"E755.sketch_text.stroke-99"),sQuery(id+"F18.wireOp",EDGE,"E755.sketch_text.stroke-100"),sQuery(id+"F18.wireOp",EDGE,"E755.sketch_text.stroke-101"),sQuery(id+"F18.wireOp",EDGE,"E755.sketch_text.stroke-102"),sQuery(id+"F18.wireOp",EDGE,"E755.sketch_text.stroke-103"),sQuery(id+"F18.wireOp",EDGE,"E755.sketch_text.stroke-104"),sQuery(id+"F18.wireOp",EDGE,"E755.sketch_text.stroke-105"),sQuery(id+"F18.wireOp",EDGE,"E755.sketch_text.stroke-106")])]});
            var Q6;
            Q6=makeQuery(id+"F19.opExtrude","SWEPT_BODY",BODY,{"disambiguationData":[OSD([sQuery(id+"F18.wireOp",EDGE,"E755.sketch_text.stroke-107"),sQuery(id+"F18.wireOp",EDGE,"E755.sketch_text.stroke-108"),sQuery(id+"F18.wireOp",EDGE,"E755.sketch_text.stroke-109"),sQuery(id+"F18.wireOp",EDGE,"E755.sketch_text.stroke-110"),sQuery(id+"F18.wireOp",EDGE,"E755.sketch_text.stroke-111"),sQuery(id+"F18.wireOp",EDGE,"E755.sketch_text.stroke-112"),sQuery(id+"F18.wireOp",EDGE,"E755.sketch_text.stroke-113"),sQuery(id+"F18.wireOp",EDGE,"E755.sketch_text.stroke-114"),sQuery(id+"F18.wireOp",EDGE,"E755.sketch_text.stroke-115"),sQuery(id+"F18.wireOp",EDGE,"E755.sketch_text.stroke-116"),sQuery(id+"F18.wireOp",EDGE,"E755.sketch_text.stroke-117"),sQuery(id+"F18.wireOp",EDGE,"E755.sketch_text.stroke-118"),sQuery(id+"F18.wireOp",EDGE,"E755.sketch_text.stroke-119"),sQuery(id+"F18.wireOp",EDGE,"E755.sketch_text.stroke-120"),sQuery(id+"F18.wireOp",EDGE,"E755.sketch_text.stroke-121"),sQuery(id+"F18.wireOp",EDGE,"E755.sketch_text.stroke-122"),sQuery(id+"F18.wireOp",EDGE,"E755.sketch_text.stroke-123"),sQuery(id+"F18.wireOp",EDGE,"E755.sketch_text.stroke-124"),sQuery(id+"F18.wireOp",EDGE,"E755.sketch_text.stroke-125")])]});
            var Q7;
            Q7=makeQuery(id+"F19.opExtrude","SWEPT_BODY",BODY,{"disambiguationData":[OSD([sQuery(id+"F18.wireOp",EDGE,"E755.sketch_text.stroke-126"),sQuery(id+"F18.wireOp",EDGE,"E755.sketch_text.stroke-127"),sQuery(id+"F18.wireOp",EDGE,"E755.sketch_text.stroke-128"),sQuery(id+"F18.wireOp",EDGE,"E755.sketch_text.stroke-129"),sQuery(id+"F18.wireOp",EDGE,"E755.sketch_text.stroke-130"),sQuery(id+"F18.wireOp",EDGE,"E755.sketch_text.stroke-131"),sQuery(id+"F18.wireOp",EDGE,"E755.sketch_text.stroke-132"),sQuery(id+"F18.wireOp",EDGE,"E755.sketch_text.stroke-133"),sQuery(id+"F18.wireOp",EDGE,"E755.sketch_text.stroke-134"),sQuery(id+"F18.wireOp",EDGE,"E755.sketch_text.stroke-135")])]});
            var Q8;
            Q8=makeQuery(id+"F19.opExtrude","SWEPT_BODY",BODY,{"disambiguationData":[OSD([sQuery(id+"F18.wireOp",EDGE,"E755.sketch_text.stroke-136"),sQuery(id+"F18.wireOp",EDGE,"E755.sketch_text.stroke-137"),sQuery(id+"F18.wireOp",EDGE,"E755.sketch_text.stroke-138"),sQuery(id+"F18.wireOp",EDGE,"E755.sketch_text.stroke-139"),sQuery(id+"F18.wireOp",EDGE,"E755.sketch_text.stroke-140"),sQuery(id+"F18.wireOp",EDGE,"E755.sketch_text.stroke-141"),sQuery(id+"F18.wireOp",EDGE,"E755.sketch_text.stroke-142"),sQuery(id+"F18.wireOp",EDGE,"E755.sketch_text.stroke-143"),sQuery(id+"F18.wireOp",EDGE,"E755.sketch_text.stroke-144"),sQuery(id+"F18.wireOp",EDGE,"E755.sketch_text.stroke-145"),sQuery(id+"F18.wireOp",EDGE,"E755.sketch_text.stroke-146"),sQuery(id+"F18.wireOp",EDGE,"E755.sketch_text.stroke-147"),sQuery(id+"F18.wireOp",EDGE,"E755.sketch_text.stroke-148"),sQuery(id+"F18.wireOp",EDGE,"E755.sketch_text.stroke-149"),sQuery(id+"F18.wireOp",EDGE,"E755.sketch_text.stroke-150"),sQuery(id+"F18.wireOp",EDGE,"E755.sketch_text.stroke-151"),sQuery(id+"F18.wireOp",EDGE,"E755.sketch_text.stroke-152"),sQuery(id+"F18.wireOp",EDGE,"E755.sketch_text.stroke-153"),sQuery(id+"F18.wireOp",EDGE,"E755.sketch_text.stroke-154"),sQuery(id+"F18.wireOp",EDGE,"E755.sketch_text.stroke-155"),sQuery(id+"F18.wireOp",EDGE,"E755.sketch_text.stroke-156"),sQuery(id+"F18.wireOp",EDGE,"E755.sketch_text.stroke-157"),sQuery(id+"F18.wireOp",EDGE,"E755.sketch_text.stroke-158"),sQuery(id+"F18.wireOp",EDGE,"E755.sketch_text.stroke-159"),sQuery(id+"F18.wireOp",EDGE,"E755.sketch_text.stroke-160")])]});
            var Q9;
            Q9=makeQuery(id+"F19.opExtrude","CAP_VERTEX",VERTEX,{"disambiguationData":[OSD([sQuery(id+"F18.wireOp",EDGE,"E755.sketch_text.stroke-82"),sQuery(id+"F18.wireOp",EDGE,"E755.sketch_text.stroke-83")])],"isStart":true});
            transform(context, id + "F28", {"entities" : qUnion([Q0, Q1, Q2, Q3, Q4, Q5, Q6, Q7, Q8]), "transformType" : TransformType.SCALE_UNIFORMLY, "scale" : 1.4, "scalePoint" : qUnion([Q9]), "makeCopy" : false});
        }
        {
            var Q0;
            Q0=makeQuery(id+"F19.opExtrude","SWEPT_BODY",BODY,{"disambiguationData":[OSD([sQuery(id+"F18.wireOp",EDGE,"E755.sketch_text.stroke-0"),sQuery(id+"F18.wireOp",EDGE,"E755.sketch_text.stroke-1"),sQuery(id+"F18.wireOp",EDGE,"E755.sketch_text.stroke-2"),sQuery(id+"F18.wireOp",EDGE,"E755.sketch_text.stroke-3"),sQuery(id+"F18.wireOp",EDGE,"E755.sketch_text.stroke-4"),sQuery(id+"F18.wireOp",EDGE,"E755.sketch_text.stroke-5"),sQuery(id+"F18.wireOp",EDGE,"E755.sketch_text.stroke-6"),sQuery(id+"F18.wireOp",EDGE,"E755.sketch_text.stroke-7"),sQuery(id+"F18.wireOp",EDGE,"E755.sketch_text.stroke-8"),sQuery(id+"F18.wireOp",EDGE,"E755.sketch_text.stroke-9"),sQuery(id+"F18.wireOp",EDGE,"E755.sketch_text.stroke-10"),sQuery(id+"F18.wireOp",EDGE,"E755.sketch_text.stroke-11"),sQuery(id+"F18.wireOp",EDGE,"E755.sketch_text.stroke-12"),sQuery(id+"F18.wireOp",EDGE,"E755.sketch_text.stroke-13"),sQuery(id+"F18.wireOp",EDGE,"E755.sketch_text.stroke-14"),sQuery(id+"F18.wireOp",EDGE,"E755.sketch_text.stroke-15"),sQuery(id+"F18.wireOp",EDGE,"E755.sketch_text.stroke-16"),sQuery(id+"F18.wireOp",EDGE,"E755.sketch_text.stroke-17"),sQuery(id+"F18.wireOp",EDGE,"E755.sketch_text.stroke-18"),sQuery(id+"F18.wireOp",EDGE,"E755.sketch_text.stroke-19"),sQuery(id+"F18.wireOp",EDGE,"E755.sketch_text.stroke-20"),sQuery(id+"F18.wireOp",EDGE,"E755.sketch_text.stroke-21"),sQuery(id+"F18.wireOp",EDGE,"E755.sketch_text.stroke-22"),sQuery(id+"F18.wireOp",EDGE,"E755.sketch_text.stroke-23"),sQuery(id+"F18.wireOp",EDGE,"E755.sketch_text.stroke-24"),sQuery(id+"F18.wireOp",EDGE,"E755.sketch_text.stroke-25"),sQuery(id+"F18.wireOp",EDGE,"E755.sketch_text.stroke-26"),sQuery(id+"F18.wireOp",EDGE,"E755.sketch_text.stroke-27"),sQuery(id+"F18.wireOp",EDGE,"E755.sketch_text.stroke-28"),sQuery(id+"F18.wireOp",EDGE,"E755.sketch_text.stroke-29"),sQuery(id+"F18.wireOp",EDGE,"E755.sketch_text.stroke-30"),sQuery(id+"F18.wireOp",EDGE,"E755.sketch_text.stroke-31"),sQuery(id+"F18.wireOp",EDGE,"E755.sketch_text.stroke-32"),sQuery(id+"F18.wireOp",EDGE,"E755.sketch_text.stroke-33"),sQuery(id+"F18.wireOp",EDGE,"E755.sketch_text.stroke-34"),sQuery(id+"F18.wireOp",EDGE,"E755.sketch_text.stroke-35")])]});
            var Q1;
            Q1=makeQuery(id+"F19.opExtrude","SWEPT_BODY",BODY,{"disambiguationData":[OSD([sQuery(id+"F18.wireOp",EDGE,"E755.sketch_text.stroke-36"),sQuery(id+"F18.wireOp",EDGE,"E755.sketch_text.stroke-37"),sQuery(id+"F18.wireOp",EDGE,"E755.sketch_text.stroke-38"),sQuery(id+"F18.wireOp",EDGE,"E755.sketch_text.stroke-39"),sQuery(id+"F18.wireOp",EDGE,"E755.sketch_text.stroke-40"),sQuery(id+"F18.wireOp",EDGE,"E755.sketch_text.stroke-41"),sQuery(id+"F18.wireOp",EDGE,"E755.sketch_text.stroke-42"),sQuery(id+"F18.wireOp",EDGE,"E755.sketch_text.stroke-43"),sQuery(id+"F18.wireOp",EDGE,"E755.sketch_text.stroke-44"),sQuery(id+"F18.wireOp",EDGE,"E755.sketch_text.stroke-45"),sQuery(id+"F18.wireOp",EDGE,"E755.sketch_text.stroke-46"),sQuery(id+"F18.wireOp",EDGE,"E755.sketch_text.stroke-47"),sQuery(id+"F18.wireOp",EDGE,"E755.sketch_text.stroke-48"),sQuery(id+"F18.wireOp",EDGE,"E755.sketch_text.stroke-49"),sQuery(id+"F18.wireOp",EDGE,"E755.sketch_text.stroke-50"),sQuery(id+"F18.wireOp",EDGE,"E755.sketch_text.stroke-51"),sQuery(id+"F18.wireOp",EDGE,"E755.sketch_text.stroke-52"),sQuery(id+"F18.wireOp",EDGE,"E755.sketch_text.stroke-53"),sQuery(id+"F18.wireOp",EDGE,"E755.sketch_text.stroke-54")])]});
            var Q2;
            Q2=makeQuery(id+"F19.opExtrude","SWEPT_BODY",BODY,{"disambiguationData":[OSD([sQuery(id+"F18.wireOp",EDGE,"E755.sketch_text.stroke-55"),sQuery(id+"F18.wireOp",EDGE,"E755.sketch_text.stroke-56"),sQuery(id+"F18.wireOp",EDGE,"E755.sketch_text.stroke-57"),sQuery(id+"F18.wireOp",EDGE,"E755.sketch_text.stroke-58"),sQuery(id+"F18.wireOp",EDGE,"E755.sketch_text.stroke-59"),sQuery(id+"F18.wireOp",EDGE,"E755.sketch_text.stroke-60"),sQuery(id+"F18.wireOp",EDGE,"E755.sketch_text.stroke-61"),sQuery(id+"F18.wireOp",EDGE,"E755.sketch_text.stroke-62"),sQuery(id+"F18.wireOp",EDGE,"E755.sketch_text.stroke-63"),sQuery(id+"F18.wireOp",EDGE,"E755.sketch_text.stroke-64"),sQuery(id+"F18.wireOp",EDGE,"E755.sketch_text.stroke-65"),sQuery(id+"F18.wireOp",EDGE,"E755.sketch_text.stroke-66"),sQuery(id+"F18.wireOp",EDGE,"E755.sketch_text.stroke-67"),sQuery(id+"F18.wireOp",EDGE,"E755.sketch_text.stroke-68"),sQuery(id+"F18.wireOp",EDGE,"E755.sketch_text.stroke-69"),sQuery(id+"F18.wireOp",EDGE,"E755.sketch_text.stroke-70"),sQuery(id+"F18.wireOp",EDGE,"E755.sketch_text.stroke-71"),sQuery(id+"F18.wireOp",EDGE,"E755.sketch_text.stroke-72"),sQuery(id+"F18.wireOp",EDGE,"E755.sketch_text.stroke-73")])]});
            var Q3;
            Q3=makeQuery(id+"F19.opExtrude","SWEPT_BODY",BODY,{"disambiguationData":[OSD([sQuery(id+"F18.wireOp",EDGE,"E755.sketch_text.stroke-74"),sQuery(id+"F18.wireOp",EDGE,"E755.sketch_text.stroke-75"),sQuery(id+"F18.wireOp",EDGE,"E755.sketch_text.stroke-76"),sQuery(id+"F18.wireOp",EDGE,"E755.sketch_text.stroke-77"),sQuery(id+"F18.wireOp",EDGE,"E755.sketch_text.stroke-78"),sQuery(id+"F18.wireOp",EDGE,"E755.sketch_text.stroke-79"),sQuery(id+"F18.wireOp",EDGE,"E755.sketch_text.stroke-80"),sQuery(id+"F18.wireOp",EDGE,"E755.sketch_text.stroke-81")])]});
            var Q4;
            Q4=makeQuery(id+"F19.opExtrude","SWEPT_BODY",BODY,{"disambiguationData":[OSD([sQuery(id+"F18.wireOp",EDGE,"E755.sketch_text.stroke-82"),sQuery(id+"F18.wireOp",EDGE,"E755.sketch_text.stroke-83"),sQuery(id+"F18.wireOp",EDGE,"E755.sketch_text.stroke-84"),sQuery(id+"F18.wireOp",EDGE,"E755.sketch_text.stroke-85"),sQuery(id+"F18.wireOp",EDGE,"E755.sketch_text.stroke-86"),sQuery(id+"F18.wireOp",EDGE,"E755.sketch_text.stroke-87"),sQuery(id+"F18.wireOp",EDGE,"E755.sketch_text.stroke-88"),sQuery(id+"F18.wireOp",EDGE,"E755.sketch_text.stroke-89"),sQuery(id+"F18.wireOp",EDGE,"E755.sketch_text.stroke-90"),sQuery(id+"F18.wireOp",EDGE,"E755.sketch_text.stroke-91")])]});
            var Q5;
            Q5=makeQuery(id+"F19.opExtrude","SWEPT_BODY",BODY,{"disambiguationData":[OSD([sQuery(id+"F18.wireOp",EDGE,"E755.sketch_text.stroke-92"),sQuery(id+"F18.wireOp",EDGE,"E755.sketch_text.stroke-93"),sQuery(id+"F18.wireOp",EDGE,"E755.sketch_text.stroke-94"),sQuery(id+"F18.wireOp",EDGE,"E755.sketch_text.stroke-95"),sQuery(id+"F18.wireOp",EDGE,"E755.sketch_text.stroke-96"),sQuery(id+"F18.wireOp",EDGE,"E755.sketch_text.stroke-97"),sQuery(id+"F18.wireOp",EDGE,"E755.sketch_text.stroke-98"),sQuery(id+"F18.wireOp",EDGE,"E755.sketch_text.stroke-99"),sQuery(id+"F18.wireOp",EDGE,"E755.sketch_text.stroke-100"),sQuery(id+"F18.wireOp",EDGE,"E755.sketch_text.stroke-101"),sQuery(id+"F18.wireOp",EDGE,"E755.sketch_text.stroke-102"),sQuery(id+"F18.wireOp",EDGE,"E755.sketch_text.stroke-103"),sQuery(id+"F18.wireOp",EDGE,"E755.sketch_text.stroke-104"),sQuery(id+"F18.wireOp",EDGE,"E755.sketch_text.stroke-105"),sQuery(id+"F18.wireOp",EDGE,"E755.sketch_text.stroke-106")])]});
            var Q6;
            Q6=makeQuery(id+"F19.opExtrude","SWEPT_BODY",BODY,{"disambiguationData":[OSD([sQuery(id+"F18.wireOp",EDGE,"E755.sketch_text.stroke-107"),sQuery(id+"F18.wireOp",EDGE,"E755.sketch_text.stroke-108"),sQuery(id+"F18.wireOp",EDGE,"E755.sketch_text.stroke-109"),sQuery(id+"F18.wireOp",EDGE,"E755.sketch_text.stroke-110"),sQuery(id+"F18.wireOp",EDGE,"E755.sketch_text.stroke-111"),sQuery(id+"F18.wireOp",EDGE,"E755.sketch_text.stroke-112"),sQuery(id+"F18.wireOp",EDGE,"E755.sketch_text.stroke-113"),sQuery(id+"F18.wireOp",EDGE,"E755.sketch_text.stroke-114"),sQuery(id+"F18.wireOp",EDGE,"E755.sketch_text.stroke-115"),sQuery(id+"F18.wireOp",EDGE,"E755.sketch_text.stroke-116"),sQuery(id+"F18.wireOp",EDGE,"E755.sketch_text.stroke-117"),sQuery(id+"F18.wireOp",EDGE,"E755.sketch_text.stroke-118"),sQuery(id+"F18.wireOp",EDGE,"E755.sketch_text.stroke-119"),sQuery(id+"F18.wireOp",EDGE,"E755.sketch_text.stroke-120"),sQuery(id+"F18.wireOp",EDGE,"E755.sketch_text.stroke-121"),sQuery(id+"F18.wireOp",EDGE,"E755.sketch_text.stroke-122"),sQuery(id+"F18.wireOp",EDGE,"E755.sketch_text.stroke-123"),sQuery(id+"F18.wireOp",EDGE,"E755.sketch_text.stroke-124"),sQuery(id+"F18.wireOp",EDGE,"E755.sketch_text.stroke-125")])]});
            var Q7;
            Q7=makeQuery(id+"F19.opExtrude","SWEPT_BODY",BODY,{"disambiguationData":[OSD([sQuery(id+"F18.wireOp",EDGE,"E755.sketch_text.stroke-126"),sQuery(id+"F18.wireOp",EDGE,"E755.sketch_text.stroke-127"),sQuery(id+"F18.wireOp",EDGE,"E755.sketch_text.stroke-128"),sQuery(id+"F18.wireOp",EDGE,"E755.sketch_text.stroke-129"),sQuery(id+"F18.wireOp",EDGE,"E755.sketch_text.stroke-130"),sQuery(id+"F18.wireOp",EDGE,"E755.sketch_text.stroke-131"),sQuery(id+"F18.wireOp",EDGE,"E755.sketch_text.stroke-132"),sQuery(id+"F18.wireOp",EDGE,"E755.sketch_text.stroke-133"),sQuery(id+"F18.wireOp",EDGE,"E755.sketch_text.stroke-134"),sQuery(id+"F18.wireOp",EDGE,"E755.sketch_text.stroke-135")])]});
            var Q8;
            Q8=makeQuery(id+"F19.opExtrude","SWEPT_BODY",BODY,{"disambiguationData":[OSD([sQuery(id+"F18.wireOp",EDGE,"E755.sketch_text.stroke-136"),sQuery(id+"F18.wireOp",EDGE,"E755.sketch_text.stroke-137"),sQuery(id+"F18.wireOp",EDGE,"E755.sketch_text.stroke-138"),sQuery(id+"F18.wireOp",EDGE,"E755.sketch_text.stroke-139"),sQuery(id+"F18.wireOp",EDGE,"E755.sketch_text.stroke-140"),sQuery(id+"F18.wireOp",EDGE,"E755.sketch_text.stroke-141"),sQuery(id+"F18.wireOp",EDGE,"E755.sketch_text.stroke-142"),sQuery(id+"F18.wireOp",EDGE,"E755.sketch_text.stroke-143"),sQuery(id+"F18.wireOp",EDGE,"E755.sketch_text.stroke-144"),sQuery(id+"F18.wireOp",EDGE,"E755.sketch_text.stroke-145"),sQuery(id+"F18.wireOp",EDGE,"E755.sketch_text.stroke-146"),sQuery(id+"F18.wireOp",EDGE,"E755.sketch_text.stroke-147"),sQuery(id+"F18.wireOp",EDGE,"E755.sketch_text.stroke-148"),sQuery(id+"F18.wireOp",EDGE,"E755.sketch_text.stroke-149"),sQuery(id+"F18.wireOp",EDGE,"E755.sketch_text.stroke-150"),sQuery(id+"F18.wireOp",EDGE,"E755.sketch_text.stroke-151"),sQuery(id+"F18.wireOp",EDGE,"E755.sketch_text.stroke-152"),sQuery(id+"F18.wireOp",EDGE,"E755.sketch_text.stroke-153"),sQuery(id+"F18.wireOp",EDGE,"E755.sketch_text.stroke-154"),sQuery(id+"F18.wireOp",EDGE,"E755.sketch_text.stroke-155"),sQuery(id+"F18.wireOp",EDGE,"E755.sketch_text.stroke-156"),sQuery(id+"F18.wireOp",EDGE,"E755.sketch_text.stroke-157"),sQuery(id+"F18.wireOp",EDGE,"E755.sketch_text.stroke-158"),sQuery(id+"F18.wireOp",EDGE,"E755.sketch_text.stroke-159"),sQuery(id+"F18.wireOp",EDGE,"E755.sketch_text.stroke-160")])]});
            transform(context, id + "F29", {"entities" : qUnion([Q0, Q1, Q2, Q3, Q4, Q5, Q6, Q7, Q8]), "transformType" : TransformType.TRANSLATION_3D, "dx" : 11.1 * mm, "dy" : 0 * mm, "dz" : 0 * mm, "makeCopy" : false});
        }
        {
            var Q0;
            Q0=makeQuery(id+"F19.opExtrude","SWEPT_BODY",BODY,{"disambiguationData":[OSD([sQuery(id+"F18.wireOp",EDGE,"E755.sketch_text.stroke-136"),sQuery(id+"F18.wireOp",EDGE,"E755.sketch_text.stroke-137"),sQuery(id+"F18.wireOp",EDGE,"E755.sketch_text.stroke-138"),sQuery(id+"F18.wireOp",EDGE,"E755.sketch_text.stroke-139"),sQuery(id+"F18.wireOp",EDGE,"E755.sketch_text.stroke-140"),sQuery(id+"F18.wireOp",EDGE,"E755.sketch_text.stroke-141"),sQuery(id+"F18.wireOp",EDGE,"E755.sketch_text.stroke-142"),sQuery(id+"F18.wireOp",EDGE,"E755.sketch_text.stroke-143"),sQuery(id+"F18.wireOp",EDGE,"E755.sketch_text.stroke-144"),sQuery(id+"F18.wireOp",EDGE,"E755.sketch_text.stroke-145"),sQuery(id+"F18.wireOp",EDGE,"E755.sketch_text.stroke-146"),sQuery(id+"F18.wireOp",EDGE,"E755.sketch_text.stroke-147"),sQuery(id+"F18.wireOp",EDGE,"E755.sketch_text.stroke-148"),sQuery(id+"F18.wireOp",EDGE,"E755.sketch_text.stroke-149"),sQuery(id+"F18.wireOp",EDGE,"E755.sketch_text.stroke-150"),sQuery(id+"F18.wireOp",EDGE,"E755.sketch_text.stroke-151"),sQuery(id+"F18.wireOp",EDGE,"E755.sketch_text.stroke-152"),sQuery(id+"F18.wireOp",EDGE,"E755.sketch_text.stroke-153"),sQuery(id+"F18.wireOp",EDGE,"E755.sketch_text.stroke-154"),sQuery(id+"F18.wireOp",EDGE,"E755.sketch_text.stroke-155"),sQuery(id+"F18.wireOp",EDGE,"E755.sketch_text.stroke-156"),sQuery(id+"F18.wireOp",EDGE,"E755.sketch_text.stroke-157"),sQuery(id+"F18.wireOp",EDGE,"E755.sketch_text.stroke-158"),sQuery(id+"F18.wireOp",EDGE,"E755.sketch_text.stroke-159"),sQuery(id+"F18.wireOp",EDGE,"E755.sketch_text.stroke-160")])]});
            transform(context, id + "F30", {"entities" : qUnion([Q0]), "transformType" : TransformType.TRANSLATION_3D, "dx" : 0 * mm, "dy" : 0.94 * mm, "dz" : 0 * mm, "makeCopy" : false});
        }
    });
